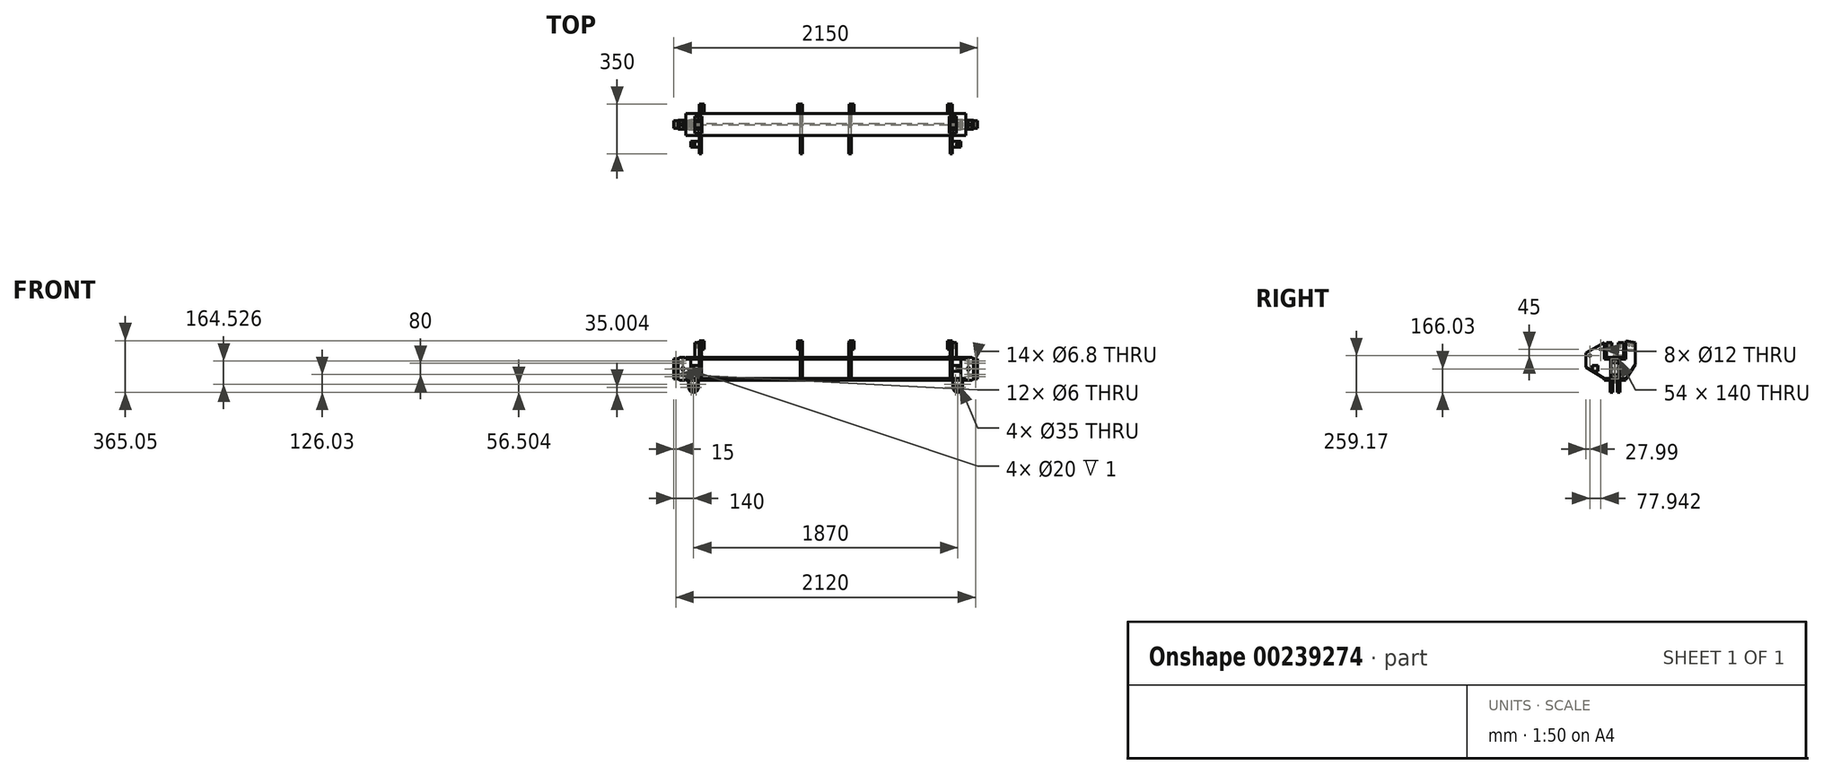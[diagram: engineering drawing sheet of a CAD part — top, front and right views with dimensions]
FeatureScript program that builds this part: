
annotation { "Feature Type Name" : "Feature", "Feature Type Description" : "" }
export const myFeature = defineFeature(function(context is Context, id is Id, definition is map)
    precondition{}
    {
        {
            var Q0;
            Q0=qCreatedBy(makeId("Right.planeOp"),FACE);
            var sketch = newSketch(context, id + "F0", { "sketchPlane" : qUnion([Q0])});
            skLineSegment(sketch, "E0.bottom", {"start": v(-77.22, 81.03) * mm, "end": v(77.22, 81.03) * mm});
            skLineSegment(sketch, "E0.top", {"start": v(-77.22, -81.03) * mm, "end": v(77.22, -81.03) * mm});
            skLineSegment(sketch, "E0.left", {"start": v(-77.22, 81.03) * mm, "end": v(-77.22, 69.47) * mm});
            skLineSegment(sketch, "E0.right", {"start": v(77.22, 81.03) * mm, "end": v(77.22, 69.47) * mm});
            skPoint(sketch, "E0.middle", {"position": v(0, 0) * mm});
            skLineSegment(sketch, "E1", {"start": v(0, 87.3) * mm, "end": v(0, -92.44) * mm, "construction": true});
            skLineSegment(sketch, "E2.0", {"start": v(-77.22, 69.47) * mm, "end": v(-16.76, 69.47) * mm});
            skLineSegment(sketch, "E3.0", {"start": v(-77.22, -69.47) * mm, "end": v(-16.76, -69.47) * mm});
            skLineSegment(sketch, "E4.0", {"start": v(-4.06, 56.77) * mm, "end": v(-4.06, -56.77) * mm});
            skLineSegment(sketch, "E5.0", {"start": v(4.06, 56.77) * mm, "end": v(4.06, -56.77) * mm});
            skLineSegment(sketch, "E6.trimOffspring", {"start": v(16.76, -69.47) * mm, "end": v(77.22, -69.47) * mm});
            skLineSegment(sketch, "E7.trimOffspring", {"start": v(16.76, 69.47) * mm, "end": v(77.22, 69.47) * mm});
            skLineSegment(sketch, "E8.trimOffspring", {"start": v(-77.22, -69.47) * mm, "end": v(-77.22, -81.03) * mm});
            skLineSegment(sketch, "E9.trimOffspring", {"start": v(77.22, -69.47) * mm, "end": v(77.22, -81.03) * mm});
            skPoint(sketch, "E10.visualSharp", {"position": v(-4.06, 69.47) * mm});
            skArc(sketch, "E10.filletArc", {"start": v(-4.06, 56.77) * mm, "mid": v(-7.78, 65.75) * mm, "end": v(-16.76, 69.47) * mm});
            skPoint(sketch, "E11.visualSharp", {"position": v(4.06, 69.47) * mm});
            skArc(sketch, "E11.filletArc", {"start": v(16.76, 69.47) * mm, "mid": v(7.78, 65.75) * mm, "end": v(4.06, 56.77) * mm});
            skPoint(sketch, "E12.visualSharp", {"position": v(4.06, -69.47) * mm});
            skArc(sketch, "E12.filletArc", {"start": v(4.06, -56.77) * mm, "mid": v(7.78, -65.75) * mm, "end": v(16.76, -69.47) * mm});
            skPoint(sketch, "E13.visualSharp", {"position": v(-4.06, -69.47) * mm});
            skArc(sketch, "E13.filletArc", {"start": v(-16.76, -69.47) * mm, "mid": v(-7.78, -65.75) * mm, "end": v(-4.06, -56.77) * mm});
            skSolve(sketch);
        }
        {
            var Q0;
            Q0=qSketchRegion(id+"F0",true);
            extrude(context, id + "F1", {"entities" : qUnion([Q0]), "endBound" : BoundingType.SYMMETRIC, "depth" : 1980 * mm});
        }
        {
            var Q0;
            Q0=makeQuery(id+"F1.opExtrude","SWEPT_FACE",FACE,{"disambiguationData":[OSD([sQuery(id+"F0.wireOp",EDGE,"E4.0")])]});
            var sketch = newSketch(context, id + "F2", { "sketchPlane" : qUnion([Q0])});
            skLineSegment(sketch, "E14", {"start": v(0, 173.84) * mm, "end": v(0, -192.2) * mm, "construction": true});
            skLineSegment(sketch, "E15.0", {"start": v(-990, 69.47) * mm, "end": v(-990, -69.47) * mm, "construction": true});
            skLineSegment(sketch, "E16.0", {"start": v(990, 69.47) * mm, "end": v(-990, 69.47) * mm, "construction": true});
            skLineSegment(sketch, "E17.0", {"start": v(990, -69.47) * mm, "end": v(-990, -69.47) * mm, "construction": true});
            skPoint(sketch, "E18.orphan", {"position": v(-990, 56.77) * mm});
            skPoint(sketch, "E19.orphan", {"position": v(-990, -56.77) * mm});
            skLineSegment(sketch, "E20.bottom", {"start": v(-990, 69.47) * mm, "end": v(-955, 69.47) * mm});
            skLineSegment(sketch, "E20.top", {"start": v(-990, -69.47) * mm, "end": v(-955, -69.47) * mm});
            skLineSegment(sketch, "E20.left", {"start": v(-990, 69.47) * mm, "end": v(-990, -69.47) * mm});
            skLineSegment(sketch, "E20.right", {"start": v(-955, 69.47) * mm, "end": v(-955, -69.47) * mm});
            skLineSegment(sketch, "E21.MirrorCS", {"start": v(990, -69.47) * mm, "end": v(955, -69.47) * mm});
            skLineSegment(sketch, "E22.MirrorCS", {"start": v(990, 69.47) * mm, "end": v(955, 69.47) * mm});
            skLineSegment(sketch, "E23.MirrorCS", {"start": v(990, 69.47) * mm, "end": v(990, -69.47) * mm});
            skLineSegment(sketch, "E24.MirrorCS", {"start": v(955, 69.47) * mm, "end": v(955, -69.47) * mm});
            skPoint(sketch, "E25.MirrorP", {"position": v(990, -56.77) * mm});
            skPoint(sketch, "E26.MirrorP", {"position": v(990, 56.77) * mm});
            skLineSegment(sketch, "E27.MirrorCS", {"start": v(990, 69.47) * mm, "end": v(990, -69.47) * mm, "construction": true});
            skSolve(sketch);
        }
        {
            var Q0;
            Q0=qSketchRegion(id+"F2",true);
            extrude(context, id + "F3", {"entities" : qUnion([Q0]), "operationType" : NewBodyOperationType.REMOVE, "endBound" : BoundingType.SYMMETRIC, "oppositeDirection" : true, "depth" : 50 * mm});
        }
        {
            var Q0;
            Q0=qCreatedBy(makeId("Front.planeOp"),FACE);
            var sketch = newSketch(context, id + "F4", { "sketchPlane" : qUnion([Q0])});
            skLineSegment(sketch, "E28", {"start": v(0, 276.7) * mm, "end": v(0, -349.05) * mm, "construction": true});
            skLineSegment(sketch, "E29.0", {"start": v(-1075, 276.7) * mm, "end": v(-1075, -349.05) * mm, "construction": true});
            skLineSegment(sketch, "E30.0", {"start": v(990, 81.03) * mm, "end": v(-1045, 81.03) * mm, "construction": true});
            skLineSegment(sketch, "E31.0", {"start": v(990, -81.03) * mm, "end": v(-1045, -81.03) * mm, "construction": true});
            skLineSegment(sketch, "E32.0", {"start": v(-955, -69.47) * mm, "end": v(-955, 69.47) * mm, "construction": true});
            skLineSegment(sketch, "E33.0", {"start": v(990, -69.47) * mm, "end": v(-990, -69.47) * mm, "construction": true});
            skLineSegment(sketch, "E34.0", {"start": v(990, 69.47) * mm, "end": v(-990, 69.47) * mm, "construction": true});
            skPoint(sketch, "E35.orphan", {"position": v(-955, 56.77) * mm});
            skPoint(sketch, "E36.orphan", {"position": v(-955, -56.77) * mm});
            skPoint(sketch, "E37.orphan", {"position": v(-990, 81.03) * mm});
            skPoint(sketch, "E38.orphan", {"position": v(-990, -81.03) * mm});
            skLineSegment(sketch, "E39", {"start": v(-990, 81.03) * mm, "end": v(-990, 69.47) * mm, "construction": true});
            skLineSegment(sketch, "E40.0", {"start": v(-1045, 81.03) * mm, "end": v(-1045, 70) * mm, "construction": true});
            skLineSegment(sketch, "E41", {"start": v(0, 0) * mm, "end": v(-1199.42, 0) * mm, "construction": true});
            skLineSegment(sketch, "E42.0", {"start": v(0, 70) * mm, "end": v(-990, 70) * mm, "construction": true});
            skLineSegment(sketch, "E43.trimOffspring", {"start": v(-1045, 70) * mm, "end": v(-1075, 70) * mm, "construction": true});
            skLineSegment(sketch, "E44.MirrorCS", {"start": v(-1045, -70) * mm, "end": v(-1075, -70) * mm, "construction": true});
            skPoint(sketch, "E45.orphan", {"position": v(-1199.42, 70) * mm});
            skPoint(sketch, "E46.orphan", {"position": v(-1199.42, -70) * mm});
            skLineSegment(sketch, "E47.trimOffspring", {"start": v(-1045, -70) * mm, "end": v(-1045, -81.03) * mm, "construction": true});
            skLineSegment(sketch, "E48.trimOffspring", {"start": v(-990, -69.47) * mm, "end": v(-990, -81.03) * mm, "construction": true});
            skLineSegment(sketch, "E49.bottom", {"start": v(-1075, 70) * mm, "end": v(-1045, 70) * mm});
            skLineSegment(sketch, "E49.top", {"start": v(-1075, -70) * mm, "end": v(-1045, -70) * mm});
            skLineSegment(sketch, "E49.left", {"start": v(-1075, 70) * mm, "end": v(-1075, -70) * mm});
            skLineSegment(sketch, "E50.bottom", {"start": v(-1045, 81.03) * mm, "end": v(-990, 81.03) * mm});
            skLineSegment(sketch, "E50.top", {"start": v(-1045, -81.03) * mm, "end": v(-990, -81.03) * mm});
            skLineSegment(sketch, "E50.left", {"start": v(-1045, 81.03) * mm, "end": v(-1045, 70) * mm});
            skLineSegment(sketch, "E50.right", {"start": v(-990, 81.03) * mm, "end": v(-990, 69.47) * mm});
            skLineSegment(sketch, "E51.bottom", {"start": v(-990, 70) * mm, "end": v(-955, 70) * mm});
            skLineSegment(sketch, "E51.top", {"start": v(-990, -69.47) * mm, "end": v(-955, -69.47) * mm});
            skLineSegment(sketch, "E51.left", {"start": v(-990, 70) * mm, "end": v(-990, 69.47) * mm});
            skLineSegment(sketch, "E51.right", {"start": v(-955, 70) * mm, "end": v(-955, -69.47) * mm});
            skLineSegment(sketch, "E52.trimOffspring", {"start": v(-990, -69.47) * mm, "end": v(-990, -81.03) * mm});
            skLineSegment(sketch, "E53.trimOffspring", {"start": v(-1045, -70) * mm, "end": v(-1045, -81.03) * mm});
            skSolve(sketch);
        }
        {
            var Q0;
            Q0=qSketchRegion(id+"F4",true);
            extrude(context, id + "F5", {"entities" : qUnion([Q0]), "endBound" : BoundingType.SYMMETRIC, "depth" : 63.5 * mm});
        }
        {
            var Q0;
            Q0=makeQuery(id+"F5.opExtrude","SWEPT_FACE",FACE,{"disambiguationData":[OSD([sQuery(id+"F4.wireOp",EDGE,"E49.bottom")])]});
            var sketch = newSketch(context, id + "F6", { "sketchPlane" : qUnion([Q0])});
            skLineSegment(sketch, "E54", {"start": v(-948.4, 0) * mm, "end": v(-1101.52, 0) * mm, "construction": true});
            skLineSegment(sketch, "E55.0", {"start": v(-1045, -31.75) * mm, "end": v(-1045, 31.75) * mm, "construction": true});
            skLineSegment(sketch, "E56.0", {"start": v(-948.4, 27) * mm, "end": v(-1101.52, 27) * mm, "construction": true});
            skLineSegment(sketch, "E57.bottom", {"start": v(-1075, 31.75) * mm, "end": v(-1045, 31.75) * mm});
            skLineSegment(sketch, "E57.top", {"start": v(-1075, 27) * mm, "end": v(-1045, 27) * mm});
            skLineSegment(sketch, "E57.left", {"start": v(-1075, 31.75) * mm, "end": v(-1075, 27) * mm});
            skLineSegment(sketch, "E57.right", {"start": v(-1045, 31.75) * mm, "end": v(-1045, 27) * mm});
            skLineSegment(sketch, "E58.MirrorCS", {"start": v(-1045, -31.75) * mm, "end": v(-1045, -27) * mm});
            skLineSegment(sketch, "E59.MirrorCS", {"start": v(-1075, -31.75) * mm, "end": v(-1075, -27) * mm});
            skLineSegment(sketch, "E60.MirrorCS", {"start": v(-1075, -27) * mm, "end": v(-1045, -27) * mm});
            skLineSegment(sketch, "E61.MirrorCS", {"start": v(-1075, -31.75) * mm, "end": v(-1045, -31.75) * mm});
            skSolve(sketch);
        }
        {
            var Q0;
            Q0=qSketchRegion(id+"F6",true);
            extrude(context, id + "F7", {"entities" : qUnion([Q0]), "operationType" : NewBodyOperationType.REMOVE, "endBound" : BoundingType.THROUGH_ALL, "oppositeDirection" : true, "depth" : 25 * mm});
        }
        {
            var Q0;
            Q0=makeQuery(id+"F5.opExtrude","SWEPT_FACE",FACE,{"disambiguationData":[OSD([sQuery(id+"F4.wireOp",EDGE,"E50.bottom")])]});
            var sketch = newSketch(context, id + "F8", { "sketchPlane" : qUnion([Q0])});
            skLineSegment(sketch, "E62.0", {"start": v(-1075, -27) * mm, "end": v(-1075, 27) * mm, "construction": true});
            skLineSegment(sketch, "E63", {"start": v(-919.6, 0) * mm, "end": v(-1088.25, 0) * mm, "construction": true});
            skPoint(sketch, "E63.endSnap0", {"position": v(-1075, 0) * mm});
            skLineSegment(sketch, "E64.0", {"start": v(-1010, -27) * mm, "end": v(-1010, 27) * mm, "construction": true});
            skPoint(sketch, "E65", {"position": v(-1010, 0) * mm});
            skSolve(sketch);
        }
        {
            var Q0;
            Q0=sQuery(id+"F8.wireOp",VERTEX,"E65");
            var Q1;
            Q1=makeQuery(id+"F5.opExtrude","SWEPT_BODY",BODY,{"disambiguationData":[OSD([sQuery(id+"F4.wireOp",EDGE,"E49.bottom"),sQuery(id+"F4.wireOp",EDGE,"E49.top"),sQuery(id+"F4.wireOp",EDGE,"E49.left"),sQuery(id+"F4.wireOp",EDGE,"E50.bottom"),sQuery(id+"F4.wireOp",EDGE,"E50.top"),sQuery(id+"F4.wireOp",EDGE,"E50.left"),sQuery(id+"F4.wireOp",EDGE,"E50.right"),sQuery(id+"F4.wireOp",EDGE,"E51.bottom"),sQuery(id+"F4.wireOp",EDGE,"E51.top"),sQuery(id+"F4.wireOp",EDGE,"E51.right"),sQuery(id+"F4.wireOp",EDGE,"E52.trimOffspring"),sQuery(id+"F4.wireOp",EDGE,"E53.trimOffspring")])]});
            hole(context, id + "F9", {"style" : HoleStyle.SIMPLE, "endStyle" : HoleEndStyle.BLIND, "standardTappedOrClearance" : lookupTablePath({ "standard" : "ISO", "size" : "6", "type" : "Drilled" }), "standardBlindInLast" : lookupTablePath({ "standard" : "ISO", "size" : "6", "type" : "Drilled" }), "holeDiameter" : 6 * mm, "holeDepth" : 125 * mm, "locations" : qUnion([Q0]), "scope" : qUnion([Q1])});
        }
        {
            var Q0;
            Q0=sQuery(id+"F8.wireOp",VERTEX,"E65");
            var Q1;
            Q1=makeQuery(id+"F5.opExtrude","SWEPT_BODY",BODY,{"disambiguationData":[OSD([sQuery(id+"F4.wireOp",EDGE,"E49.bottom"),sQuery(id+"F4.wireOp",EDGE,"E49.top"),sQuery(id+"F4.wireOp",EDGE,"E49.left"),sQuery(id+"F4.wireOp",EDGE,"E50.bottom"),sQuery(id+"F4.wireOp",EDGE,"E50.top"),sQuery(id+"F4.wireOp",EDGE,"E50.left"),sQuery(id+"F4.wireOp",EDGE,"E50.right"),sQuery(id+"F4.wireOp",EDGE,"E51.bottom"),sQuery(id+"F4.wireOp",EDGE,"E51.top"),sQuery(id+"F4.wireOp",EDGE,"E51.right"),sQuery(id+"F4.wireOp",EDGE,"E52.trimOffspring"),sQuery(id+"F4.wireOp",EDGE,"E53.trimOffspring")])]});
            hole(context, id + "F10", {"style" : HoleStyle.SIMPLE, "endStyle" : HoleEndStyle.BLIND, "standardTappedOrClearance" : lookupTablePath({ "standard" : "ANSI", "engagement" : "75%", "pitch" : "13 tpi", "size" : "1/2", "type" : "Tapped" }), "standardBlindInLast" : lookupTablePath({ "standard" : "ANSI", "engagement" : "75%", "pitch" : "13 tpi", "size" : "1/2", "type" : "Tapped" }), "holeDiameter" : 10.72 * mm, "holeDepth" : 15 * mm, "locations" : qUnion([Q0]), "scope" : qUnion([Q1]), "majorDiameter" : 12.7 * mm});
        }
        {
            var Q0;
            {var subQ0=sQuery(id+"F4.wireOp",EDGE,"E50.bottom");Q0=makeQuery(id+"F8.imprint","IMPRINT",FACE,{"disambiguationData":[TD([[makeQuery(id+"F8.imprint","IMPRINT",EDGE,{"derivedFrom":makeQuery(id+"F5.opExtrude","CAP_EDGE",EDGE,{"disambiguationData":[OSD([subQ0])],"isStart":true})}),-1.0]])]});}
            var sketch = newSketch(context, id + "F11", { "sketchPlane" : qUnion([Q0])});
            skPoint(sketch, "E66.0", {"position": v(-1010, 0) * mm});
            skCircle(sketch, "E67", {"center": v(-1010, 0) * mm, "radius": 10 * mm});
            skSolve(sketch);
        }
        {
            var Q0;
            Q0=qSketchRegion(id+"F11",true);
            extrude(context, id + "F12", {"entities" : qUnion([Q0]), "operationType" : NewBodyOperationType.REMOVE, "oppositeDirection" : true, "depth" : 1 * mm});
        }
        {
            var Q0;
            Q0=makeQuery(id+"F5.opExtrude","SWEPT_EDGE",EDGE,{"disambiguationData":[OSD([sQuery(id+"F4.wireOp",EDGE,"E50.bottom"),sQuery(id+"F4.wireOp",EDGE,"E50.left")])]});
            var Q1;
            Q1=makeQuery(id+"F7.boolean.opBoolean","INTERSECT",EDGE,{"derivedFrom":[makeQuery(id+"F7.opExtrude","SWEPT_FACE",FACE,{"disambiguationData":[OSD([sQuery(id+"F6.wireOp",EDGE,"E57.right")])]}),makeQuery(id+"F7.opExtrude","SWEPT_FACE",FACE,{"disambiguationData":[OSD([sQuery(id+"F6.wireOp",EDGE,"E58.MirrorCS")])]})]});
            chamfer(context, id + "F13", {"entities" : qUnion([Q0, Q1]), "width" : 11 * mm, "tangentPropagation" : true});
        }
        {
            var Q0;
            Q0=makeQuery(id+"F5.opExtrude","CAP_FACE",FACE,{"disambiguationData":[OSD([sQuery(id+"F4.wireOp",EDGE,"E49.bottom"),sQuery(id+"F4.wireOp",EDGE,"E49.top"),sQuery(id+"F4.wireOp",EDGE,"E49.left"),sQuery(id+"F4.wireOp",EDGE,"E50.bottom"),sQuery(id+"F4.wireOp",EDGE,"E50.top"),sQuery(id+"F4.wireOp",EDGE,"E50.left"),sQuery(id+"F4.wireOp",EDGE,"E50.right"),sQuery(id+"F4.wireOp",EDGE,"E51.bottom"),sQuery(id+"F4.wireOp",EDGE,"E51.top"),sQuery(id+"F4.wireOp",EDGE,"E51.right"),sQuery(id+"F4.wireOp",EDGE,"E52.trimOffspring"),sQuery(id+"F4.wireOp",EDGE,"E53.trimOffspring")])],"isStart":false});
            var sketch = newSketch(context, id + "F14", { "sketchPlane" : qUnion([Q0])});
            skLineSegment(sketch, "E68", {"start": v(-947.26, 0.27) * mm, "end": v(-1104.17, 0.27) * mm, "construction": true});
            skPoint(sketch, "E68.startSnap0", {"position": v(-955, 0.27) * mm});
            skLineSegment(sketch, "E69.0", {"start": v(-1075, -70) * mm, "end": v(-1075, 70) * mm, "construction": true});
            skLineSegment(sketch, "E70.0", {"start": v(-1010, -70) * mm, "end": v(-1010, 70) * mm, "construction": true});
            skPoint(sketch, "E71", {"position": v(-1010, 0.27) * mm});
            skSolve(sketch);
        }
        {
            var Q0;
            Q0=sQuery(id+"F14.wireOp",VERTEX,"E71");
            var Q1;
            Q1=makeQuery(id+"F5.opExtrude","SWEPT_BODY",BODY,{"disambiguationData":[OSD([sQuery(id+"F4.wireOp",EDGE,"E49.bottom"),sQuery(id+"F4.wireOp",EDGE,"E49.top"),sQuery(id+"F4.wireOp",EDGE,"E49.left"),sQuery(id+"F4.wireOp",EDGE,"E50.bottom"),sQuery(id+"F4.wireOp",EDGE,"E50.top"),sQuery(id+"F4.wireOp",EDGE,"E50.left"),sQuery(id+"F4.wireOp",EDGE,"E50.right"),sQuery(id+"F4.wireOp",EDGE,"E51.bottom"),sQuery(id+"F4.wireOp",EDGE,"E51.top"),sQuery(id+"F4.wireOp",EDGE,"E51.right"),sQuery(id+"F4.wireOp",EDGE,"E52.trimOffspring"),sQuery(id+"F4.wireOp",EDGE,"E53.trimOffspring")])]});
            hole(context, id + "F15", {"style" : HoleStyle.SIMPLE, "endStyle" : HoleEndStyle.BLIND, "standardTappedOrClearance" : lookupTablePath({ "standard" : "ANSI", "engagement" : "75%", "pitch" : "13 tpi", "size" : "1/2", "type" : "Tapped" }), "standardBlindInLast" : lookupTablePath({ "standard" : "ANSI", "engagement" : "75%", "pitch" : "13 tpi", "size" : "1/2", "type" : "Tapped" }), "holeDiameter" : 10.72 * mm, "holeDepth" : 15 * mm, "locations" : qUnion([Q0]), "scope" : qUnion([Q1]), "majorDiameter" : 12.7 * mm});
        }
        {
            var Q0;
            Q0=sQuery(id+"F14.wireOp",VERTEX,"E71");
            var Q1;
            Q1=makeQuery(id+"F5.opExtrude","SWEPT_BODY",BODY,{"disambiguationData":[OSD([sQuery(id+"F4.wireOp",EDGE,"E49.bottom"),sQuery(id+"F4.wireOp",EDGE,"E49.top"),sQuery(id+"F4.wireOp",EDGE,"E49.left"),sQuery(id+"F4.wireOp",EDGE,"E50.bottom"),sQuery(id+"F4.wireOp",EDGE,"E50.top"),sQuery(id+"F4.wireOp",EDGE,"E50.left"),sQuery(id+"F4.wireOp",EDGE,"E50.right"),sQuery(id+"F4.wireOp",EDGE,"E51.bottom"),sQuery(id+"F4.wireOp",EDGE,"E51.top"),sQuery(id+"F4.wireOp",EDGE,"E51.right"),sQuery(id+"F4.wireOp",EDGE,"E52.trimOffspring"),sQuery(id+"F4.wireOp",EDGE,"E53.trimOffspring")])]});
            hole(context, id + "F16", {"style" : HoleStyle.SIMPLE, "endStyle" : HoleEndStyle.THROUGH, "standardTappedOrClearance" : lookupTablePath({ "standard" : "ISO", "size" : "6", "type" : "Drilled" }), "standardBlindInLast" : lookupTablePath({ "standard" : "ISO", "size" : "6", "type" : "Drilled" }), "holeDiameter" : 6 * mm, "locations" : qUnion([Q0]), "scope" : qUnion([Q1]), "isTappedThrough" : true});
        }
        {
            var Q0;
            {var subQ4=sQuery(id+"F4.wireOp",EDGE,"E50.right");Q0=makeQuery(id+"F14.imprint","IMPRINT",FACE,{"disambiguationData":[TD([[makeQuery(id+"F14.imprint","IMPRINT",EDGE,{"derivedFrom":makeQuery(id+"F5.opExtrude","CAP_EDGE",EDGE,{"disambiguationData":[OSD([subQ4])],"isStart":false})}),-1.0]])]});}
            var sketch = newSketch(context, id + "F17", { "sketchPlane" : qUnion([Q0])});
            skCircle(sketch, "E72", {"center": v(-1010, 0.27) * mm, "radius": 10 * mm});
            skSolve(sketch);
        }
        {
            var Q0;
            Q0=qSketchRegion(id+"F17",true);
            extrude(context, id + "F18", {"entities" : qUnion([Q0]), "operationType" : NewBodyOperationType.REMOVE, "oppositeDirection" : true, "depth" : 1 * mm});
        }
        {
            var Q0;
            Q0=makeQuery(id+"F5.opExtrude","CAP_FACE",FACE,{"disambiguationData":[OSD([sQuery(id+"F4.wireOp",EDGE,"E49.bottom"),sQuery(id+"F4.wireOp",EDGE,"E49.top"),sQuery(id+"F4.wireOp",EDGE,"E49.left"),sQuery(id+"F4.wireOp",EDGE,"E50.bottom"),sQuery(id+"F4.wireOp",EDGE,"E50.top"),sQuery(id+"F4.wireOp",EDGE,"E50.left"),sQuery(id+"F4.wireOp",EDGE,"E50.right"),sQuery(id+"F4.wireOp",EDGE,"E51.bottom"),sQuery(id+"F4.wireOp",EDGE,"E51.top"),sQuery(id+"F4.wireOp",EDGE,"E51.right"),sQuery(id+"F4.wireOp",EDGE,"E52.trimOffspring"),sQuery(id+"F4.wireOp",EDGE,"E53.trimOffspring")])],"isStart":true});
            var sketch = newSketch(context, id + "F19", { "sketchPlane" : qUnion([Q0])});
            skCircle(sketch, "E73.0", {"center": v(1010, 0.27) * mm, "radius": 10 * mm, "construction": true});
            skCircle(sketch, "E74", {"center": v(1010, 0.27) * mm, "radius": 10 * mm});
            skSolve(sketch);
        }
        {
            var Q0;
            Q0=qSketchRegion(id+"F19",true);
            extrude(context, id + "F20", {"entities" : qUnion([Q0]), "operationType" : NewBodyOperationType.REMOVE, "oppositeDirection" : true, "depth" : 1 * mm});
        }
        {
            var Q0;
            Q0=sQuery(id+"F19.wireOp",VERTEX,"E73.0.center");
            var Q1;
            Q1=makeQuery(id+"F5.opExtrude","SWEPT_BODY",BODY,{"disambiguationData":[OSD([sQuery(id+"F4.wireOp",EDGE,"E49.bottom"),sQuery(id+"F4.wireOp",EDGE,"E49.top"),sQuery(id+"F4.wireOp",EDGE,"E49.left"),sQuery(id+"F4.wireOp",EDGE,"E50.bottom"),sQuery(id+"F4.wireOp",EDGE,"E50.top"),sQuery(id+"F4.wireOp",EDGE,"E50.left"),sQuery(id+"F4.wireOp",EDGE,"E50.right"),sQuery(id+"F4.wireOp",EDGE,"E51.bottom"),sQuery(id+"F4.wireOp",EDGE,"E51.top"),sQuery(id+"F4.wireOp",EDGE,"E51.right"),sQuery(id+"F4.wireOp",EDGE,"E52.trimOffspring"),sQuery(id+"F4.wireOp",EDGE,"E53.trimOffspring")])]});
            hole(context, id + "F21", {"style" : HoleStyle.SIMPLE, "endStyle" : HoleEndStyle.BLIND, "standardTappedOrClearance" : lookupTablePath({ "standard" : "ANSI", "engagement" : "75%", "pitch" : "13 tpi", "size" : "1/2", "type" : "Tapped" }), "standardBlindInLast" : lookupTablePath({ "standard" : "ANSI", "engagement" : "75%", "pitch" : "13 tpi", "size" : "1/2", "type" : "Tapped" }), "holeDiameter" : 10.72 * mm, "holeDepth" : 15 * mm, "locations" : qUnion([Q0]), "scope" : qUnion([Q1]), "majorDiameter" : 12.7 * mm});
        }
        {
            var Q0;
            Q0=makeQuery(id+"F7.boolean.opBoolean","COPY",FACE,{"derivedFrom":makeQuery(id+"F7.opExtrude","SWEPT_FACE",FACE,{"disambiguationData":[OSD([sQuery(id+"F6.wireOp",EDGE,"E60.MirrorCS")])]})});
            var sketch = newSketch(context, id + "F22", { "sketchPlane" : qUnion([Q0])});
            skLineSegment(sketch, "E75.0", {"start": v(-1075, -70) * mm, "end": v(-1075, 70) * mm, "construction": true});
            skLineSegment(sketch, "E76.0", {"start": v(-1060, -70) * mm, "end": v(-1060, 70) * mm, "construction": true});
            skLineSegment(sketch, "E77", {"start": v(-1060, 0) * mm, "end": v(-1136.9, 0) * mm, "construction": true});
            skLineSegment(sketch, "E78.0", {"start": v(-1060, 55) * mm, "end": v(-1136.9, 55) * mm, "construction": true});
            skLineSegment(sketch, "E79.0", {"start": v(-1060, -55) * mm, "end": v(-1136.9, -55) * mm, "construction": true});
            skPoint(sketch, "E80", {"position": v(-1060, 55) * mm});
            skPoint(sketch, "E81", {"position": v(-1060, 0) * mm});
            skPoint(sketch, "E82", {"position": v(-1060, -55) * mm});
            skSolve(sketch);
        }
        {
            var Q0;
            Q0=sQuery(id+"F22.wireOp",VERTEX,"E80");
            var Q1;
            Q1=sQuery(id+"F22.wireOp",VERTEX,"E81");
            var Q2;
            Q2=sQuery(id+"F22.wireOp",VERTEX,"E82");
            var Q3;
            Q3=makeQuery(id+"F5.opExtrude","SWEPT_BODY",BODY,{"disambiguationData":[OSD([sQuery(id+"F4.wireOp",EDGE,"E49.bottom"),sQuery(id+"F4.wireOp",EDGE,"E49.top"),sQuery(id+"F4.wireOp",EDGE,"E49.left"),sQuery(id+"F4.wireOp",EDGE,"E50.bottom"),sQuery(id+"F4.wireOp",EDGE,"E50.top"),sQuery(id+"F4.wireOp",EDGE,"E50.left"),sQuery(id+"F4.wireOp",EDGE,"E50.right"),sQuery(id+"F4.wireOp",EDGE,"E51.bottom"),sQuery(id+"F4.wireOp",EDGE,"E51.top"),sQuery(id+"F4.wireOp",EDGE,"E51.right"),sQuery(id+"F4.wireOp",EDGE,"E52.trimOffspring"),sQuery(id+"F4.wireOp",EDGE,"E53.trimOffspring")])]});
            hole(context, id + "F23", {"style" : HoleStyle.SIMPLE, "endStyle" : HoleEndStyle.THROUGH, "standardTappedOrClearance" : lookupTablePath({ "standard" : "ISO", "engagement" : "75%", "pitch" : "1.25 mm", "size" : "M8", "type" : "Tapped" }), "standardBlindInLast" : lookupTablePath({ "standard" : "ISO", "engagement" : "75%", "pitch" : "1.25 mm", "size" : "M8", "type" : "Tapped" }), "holeDiameter" : 6.8 * mm, "locations" : qUnion([Q0, Q1, Q2]), "scope" : qUnion([Q3]), "isTappedThrough" : true, "majorDiameter" : 8 * mm, "showTappedDepth" : true});
        }
        {
            var Q0;
            Q0=makeQuery(id+"F7.boolean.opBoolean","COPY",FACE,{"derivedFrom":makeQuery(id+"F7.opExtrude","SWEPT_FACE",FACE,{"disambiguationData":[OSD([sQuery(id+"F6.wireOp",EDGE,"E60.MirrorCS")])]})});
            var sketch = newSketch(context, id + "F24", { "sketchPlane" : qUnion([Q0])});
            skLineSegment(sketch, "E83.0", {"start": v(-1060, 0) * mm, "end": v(-1136.9, 0) * mm, "construction": true});
            skLineSegment(sketch, "E84.0", {"start": v(-1060, -70) * mm, "end": v(-1060, 70) * mm, "construction": true});
            skLineSegment(sketch, "E85.0", {"start": v(-1060, 40) * mm, "end": v(-1136.9, 40) * mm, "construction": true});
            skPoint(sketch, "E86", {"position": v(-1060, 40) * mm});
            skPoint(sketch, "E87.MirrorP", {"position": v(-1060, -40) * mm});
            skSolve(sketch);
        }
        {
            var Q0;
            Q0=sQuery(id+"F24.wireOp",VERTEX,"E86");
            var Q1;
            Q1=sQuery(id+"F24.wireOp",VERTEX,"E87.MirrorP");
            var Q2;
            Q2=makeQuery(id+"F5.opExtrude","SWEPT_BODY",BODY,{"disambiguationData":[OSD([sQuery(id+"F4.wireOp",EDGE,"E49.bottom"),sQuery(id+"F4.wireOp",EDGE,"E49.top"),sQuery(id+"F4.wireOp",EDGE,"E49.left"),sQuery(id+"F4.wireOp",EDGE,"E50.bottom"),sQuery(id+"F4.wireOp",EDGE,"E50.top"),sQuery(id+"F4.wireOp",EDGE,"E50.left"),sQuery(id+"F4.wireOp",EDGE,"E50.right"),sQuery(id+"F4.wireOp",EDGE,"E51.bottom"),sQuery(id+"F4.wireOp",EDGE,"E51.top"),sQuery(id+"F4.wireOp",EDGE,"E51.right"),sQuery(id+"F4.wireOp",EDGE,"E52.trimOffspring"),sQuery(id+"F4.wireOp",EDGE,"E53.trimOffspring")])]});
            hole(context, id + "F25", {"style" : HoleStyle.SIMPLE, "endStyle" : HoleEndStyle.THROUGH, "standardTappedOrClearance" : lookupTablePath({ "standard" : "ISO", "size" : "6", "type" : "Drilled" }), "standardBlindInLast" : lookupTablePath({ "standard" : "ISO", "size" : "6", "type" : "Drilled" }), "holeDiameter" : 6 * mm, "locations" : qUnion([Q0, Q1]), "scope" : qUnion([Q2]), "isTappedThrough" : true});
        }
        {
            var Q0;
            Q0=makeQuery(id+"F5.opExtrude","SWEPT_FACE",FACE,{"disambiguationData":[OSD([sQuery(id+"F4.wireOp",EDGE,"E49.left")])]});
            var sketch = newSketch(context, id + "F26", { "sketchPlane" : qUnion([Q0])});
            skLineSegment(sketch, "E88.0.0", {"start": v(-27, -70) * mm, "end": v(27, -70) * mm, "construction": true});
            skLineSegment(sketch, "E88.0.1", {"start": v(27, -70) * mm, "end": v(27, 70) * mm, "construction": true});
            skLineSegment(sketch, "E88.0.2", {"start": v(27, 70) * mm, "end": v(-27, 70) * mm, "construction": true});
            skLineSegment(sketch, "E88.0.3", {"start": v(-27, 70) * mm, "end": v(-27, -70) * mm, "construction": true});
            skLineSegment(sketch, "E89", {"start": v(-27, 0) * mm, "end": v(56.48, 0) * mm, "construction": true});
            skPoint(sketch, "E89.endSnap0", {"position": v(-27, 0) * mm});
            skLineSegment(sketch, "E90", {"start": v(0, 96.87) * mm, "end": v(0, -94.28) * mm, "construction": true});
            skLineSegment(sketch, "E91.0", {"start": v(-27, -40) * mm, "end": v(56.48, -40) * mm, "construction": true});
            skPoint(sketch, "E92", {"position": v(0, -40) * mm});
            skPoint(sketch, "E93.MirrorP", {"position": v(0, 40) * mm});
            skSolve(sketch);
        }
        {
            var Q0;
            Q0=sQuery(id+"F26.wireOp",VERTEX,"E93.MirrorP");
            var Q1;
            Q1=sQuery(id+"F26.wireOp",VERTEX,"E92");
            var Q2;
            Q2=makeQuery(id+"F5.opExtrude","SWEPT_BODY",BODY,{"disambiguationData":[OSD([sQuery(id+"F4.wireOp",EDGE,"E49.bottom"),sQuery(id+"F4.wireOp",EDGE,"E49.top"),sQuery(id+"F4.wireOp",EDGE,"E49.left"),sQuery(id+"F4.wireOp",EDGE,"E50.bottom"),sQuery(id+"F4.wireOp",EDGE,"E50.top"),sQuery(id+"F4.wireOp",EDGE,"E50.left"),sQuery(id+"F4.wireOp",EDGE,"E50.right"),sQuery(id+"F4.wireOp",EDGE,"E51.bottom"),sQuery(id+"F4.wireOp",EDGE,"E51.top"),sQuery(id+"F4.wireOp",EDGE,"E51.right"),sQuery(id+"F4.wireOp",EDGE,"E52.trimOffspring"),sQuery(id+"F4.wireOp",EDGE,"E53.trimOffspring")])]});
            hole(context, id + "F27", {"style" : HoleStyle.SIMPLE, "endStyle" : HoleEndStyle.BLIND, "standardTappedOrClearance" : lookupTablePath({ "standard" : "ISO", "size" : "6", "type" : "Drilled" }), "standardBlindInLast" : lookupTablePath({ "standard" : "ISO", "size" : "6", "type" : "Drilled" }), "holeDiameter" : 6 * mm, "holeDepth" : 65 * mm, "locations" : qUnion([Q0, Q1]), "scope" : qUnion([Q2])});
        }
        {
            var Q0;
            Q0=sQuery(id+"F26.wireOp",VERTEX,"E93.MirrorP");
            var Q1;
            Q1=sQuery(id+"F26.wireOp",VERTEX,"E92");
            var Q2;
            Q2=makeQuery(id+"F5.opExtrude","SWEPT_BODY",BODY,{"disambiguationData":[OSD([sQuery(id+"F4.wireOp",EDGE,"E49.bottom"),sQuery(id+"F4.wireOp",EDGE,"E49.top"),sQuery(id+"F4.wireOp",EDGE,"E49.left"),sQuery(id+"F4.wireOp",EDGE,"E50.bottom"),sQuery(id+"F4.wireOp",EDGE,"E50.top"),sQuery(id+"F4.wireOp",EDGE,"E50.left"),sQuery(id+"F4.wireOp",EDGE,"E50.right"),sQuery(id+"F4.wireOp",EDGE,"E51.bottom"),sQuery(id+"F4.wireOp",EDGE,"E51.top"),sQuery(id+"F4.wireOp",EDGE,"E51.right"),sQuery(id+"F4.wireOp",EDGE,"E52.trimOffspring"),sQuery(id+"F4.wireOp",EDGE,"E53.trimOffspring")])]});
            hole(context, id + "F28", {"style" : HoleStyle.SIMPLE, "endStyle" : HoleEndStyle.BLIND, "standardTappedOrClearance" : lookupTablePath({ "standard" : "ISO", "engagement" : "75%", "pitch" : "1.25 mm", "size" : "M8", "type" : "Tapped" }), "standardBlindInLast" : lookupTablePath({ "standard" : "ISO", "engagement" : "75%", "pitch" : "1.25 mm", "size" : "M8", "type" : "Tapped" }), "holeDiameter" : 6.8 * mm, "holeDepth" : 12 * mm, "locations" : qUnion([Q0, Q1]), "scope" : qUnion([Q2]), "majorDiameter" : 8 * mm});
        }
        {
            var Q0;
            Q0=makeQuery(id+"F5.opExtrude","SWEPT_BODY",BODY,{"disambiguationData":[OSD([sQuery(id+"F4.wireOp",EDGE,"E49.bottom"),sQuery(id+"F4.wireOp",EDGE,"E49.top"),sQuery(id+"F4.wireOp",EDGE,"E49.left"),sQuery(id+"F4.wireOp",EDGE,"E50.bottom"),sQuery(id+"F4.wireOp",EDGE,"E50.top"),sQuery(id+"F4.wireOp",EDGE,"E50.left"),sQuery(id+"F4.wireOp",EDGE,"E50.right"),sQuery(id+"F4.wireOp",EDGE,"E51.bottom"),sQuery(id+"F4.wireOp",EDGE,"E51.top"),sQuery(id+"F4.wireOp",EDGE,"E51.right"),sQuery(id+"F4.wireOp",EDGE,"E52.trimOffspring"),sQuery(id+"F4.wireOp",EDGE,"E53.trimOffspring")])]});
            var Q1;
            Q1=qCreatedBy(makeId("Right.planeOp"),FACE);
            mirror(context, id + "F29", {"entities" : qUnion([Q0]), "mirrorPlane" : qUnion([Q1])});
        }
        {
            var Q0;
            Q0=qCreatedBy(makeId("Front.planeOp"),FACE);
            var sketch = newSketch(context, id + "F30", { "sketchPlane" : qUnion([Q0])});
            skLineSegment(sketch, "E94", {"start": v(0, 217.37) * mm, "end": v(0, -483.51) * mm, "construction": true});
            skLineSegment(sketch, "E95.0", {"start": v(-935, 217.37) * mm, "end": v(-935, -483.51) * mm, "construction": true});
            skLineSegment(sketch, "E96.0.0", {"start": v(-990, -69.47) * mm, "end": v(-990, -81.03) * mm, "construction": true});
            skLineSegment(sketch, "E96.0.1", {"start": v(-990, -81.03) * mm, "end": v(-900, -81.03) * mm});
            skLineSegment(sketch, "E96.0.2", {"start": v(990, -81.03) * mm, "end": v(990, -69.47) * mm, "construction": true});
            skLineSegment(sketch, "E96.0.3", {"start": v(990, -69.47) * mm, "end": v(-990, -69.47) * mm, "construction": true});
            skLineSegment(sketch, "E97.0", {"start": v(-990, -131.03) * mm, "end": v(990, -131.03) * mm, "construction": true});
            skCircle(sketch, "E98", {"center": v(-935, -131.03) * mm, "radius": 17.5 * mm});
            skArc(sketch, "E99", {"start": v(-970, -131.03) * mm, "mid": v(-935, -166.03) * mm, "end": v(-900, -131.03) * mm});
            skLineSegment(sketch, "E100", {"start": v(-970, -131.03) * mm, "end": v(-970, -81.03) * mm});
            skLineSegment(sketch, "E101", {"start": v(-900, -131.03) * mm, "end": v(-900, -81.03) * mm});
            skLineSegment(sketch, "E102.trimOffspring", {"start": v(0, -81.03) * mm, "end": v(990, -81.03) * mm});
            skLineSegment(sketch, "E103", {"start": v(-935, -166.03) * mm, "end": v(-989.6, -166.03) * mm, "construction": true});
            skLineSegment(sketch, "E104.0", {"start": v(-935, -144.53) * mm, "end": v(-989.6, -144.53) * mm, "construction": true});
            skLineSegment(sketch, "E105.0", {"start": v(-990, -109.53) * mm, "end": v(990, -109.53) * mm, "construction": true});
            skLineSegment(sketch, "E106.0", {"start": v(-953, 217.37) * mm, "end": v(-953, -483.51) * mm, "construction": true});
            skPoint(sketch, "E107", {"position": v(-953, -109.53) * mm});
            skPoint(sketch, "E108.MirrorP", {"position": v(-917, -109.53) * mm});
            skSolve(sketch);
        }
        {
            var Q0;
            Q0=qSketchRegion(id+"F30",true);
            extrude(context, id + "F31", {"entities" : qUnion([Q0]), "endBound" : BoundingType.SYMMETRIC, "depth" : 70 * mm});
        }
        {
            var Q0;
            Q0=makeQuery(id+"F31.opExtrude","CAP_FACE",FACE,{"disambiguationData":[OSD([sQuery(id+"F30.wireOp",EDGE,"E96.0.1"),sQuery(id+"F30.wireOp",EDGE,"E98"),sQuery(id+"F30.wireOp",EDGE,"E99"),sQuery(id+"F30.wireOp",EDGE,"E100"),sQuery(id+"F30.wireOp",EDGE,"E101")])],"isStart":false});
            var sketch = newSketch(context, id + "F32", { "sketchPlane" : qUnion([Q0])});
            skPoint(sketch, "E109.0", {"position": v(-953, -109.53) * mm});
            skPoint(sketch, "E110.0", {"position": v(-917, -109.53) * mm});
            skSolve(sketch);
        }
        {
            var Q0;
            Q0=sQuery(id+"F32.wireOp",VERTEX,"E109.0");
            var Q1;
            Q1=sQuery(id+"F32.wireOp",VERTEX,"E110.0");
            var Q2;
            Q2=makeQuery(id+"F31.opExtrude","SWEPT_BODY",BODY,{"disambiguationData":[OSD([sQuery(id+"F30.wireOp",EDGE,"E96.0.1"),sQuery(id+"F30.wireOp",EDGE,"E98"),sQuery(id+"F30.wireOp",EDGE,"E99"),sQuery(id+"F30.wireOp",EDGE,"E100"),sQuery(id+"F30.wireOp",EDGE,"E101")])]});
            hole(context, id + "F33", {"style" : HoleStyle.SIMPLE, "endStyle" : HoleEndStyle.THROUGH, "standardTappedOrClearance" : lookupTablePath({ "standard" : "ISO", "engagement" : "75%", "pitch" : "1.25 mm", "size" : "M8", "type" : "Tapped" }), "standardBlindInLast" : lookupTablePath({ "standard" : "ISO", "engagement" : "75%", "pitch" : "1.25 mm", "size" : "M8", "type" : "Tapped" }), "holeDiameter" : 6.8 * mm, "locations" : qUnion([Q0, Q1]), "scope" : qUnion([Q2]), "isTappedThrough" : true, "majorDiameter" : 8 * mm, "showTappedDepth" : true});
        }
        {
            var Q0;
            Q0=makeQuery(id+"F31.opExtrude","SWEPT_FACE",FACE,{"disambiguationData":[OSD([sQuery(id+"F30.wireOp",EDGE,"E101")])]});
            var sketch = newSketch(context, id + "F34", { "sketchPlane" : qUnion([Q0])});
            skLineSegment(sketch, "E111.0", {"start": v(-35, -81.03) * mm, "end": v(35, -81.03) * mm, "construction": true});
            skLineSegment(sketch, "E112", {"start": v(0, -81.03) * mm, "end": v(0, -181.86) * mm, "construction": true});
            skPoint(sketch, "E112.endSnap0", {"position": v(0, -81.03) * mm});
            skLineSegment(sketch, "E113.0", {"start": v(-15.5, -81.03) * mm, "end": v(-15.5, -181.86) * mm, "construction": true});
            skLineSegment(sketch, "E114", {"start": v(35, -166.03) * mm, "end": v(-35, -166.03) * mm, "construction": true});
            skLineSegment(sketch, "E115.0", {"start": v(35, -148.53) * mm, "end": v(35, -113.53) * mm, "construction": true});
            skLineSegment(sketch, "E116", {"start": v(35, -131.03) * mm, "end": v(-53.23, -131.03) * mm, "construction": true});
            skLineSegment(sketch, "E117.0", {"start": v(35, -87.03) * mm, "end": v(-53.23, -87.03) * mm, "construction": true});
            skLineSegment(sketch, "E118.bottom", {"start": v(-15.5, -166.03) * mm, "end": v(15.5, -166.03) * mm});
            skLineSegment(sketch, "E118.top", {"start": v(-15.5, -87.03) * mm, "end": v(15.5, -87.03) * mm});
            skLineSegment(sketch, "E118.left", {"start": v(-15.5, -166.03) * mm, "end": v(-15.5, -87.03) * mm});
            skLineSegment(sketch, "E118.right", {"start": v(15.5, -166.03) * mm, "end": v(15.5, -87.03) * mm});
            skSolve(sketch);
        }
        {
            var Q0;
            Q0=qSketchRegion(id+"F34",true);
            extrude(context, id + "F35", {"entities" : qUnion([Q0]), "operationType" : NewBodyOperationType.REMOVE, "endBound" : BoundingType.THROUGH_ALL, "oppositeDirection" : true, "depth" : 25 * mm});
        }
        {
            var Q0;
            Q0=makeQuery(id+"F35.boolean.opBoolean","COPY",EDGE,{"derivedFrom":makeQuery(id+"F35.opExtrude","SWEPT_EDGE",EDGE,{"disambiguationData":[OSD([sQuery(id+"F34.wireOp",EDGE,"E118.top"),sQuery(id+"F34.wireOp",EDGE,"E118.right")])]})});
            var Q1;
            Q1=makeQuery(id+"F35.boolean.opBoolean","COPY",EDGE,{"derivedFrom":makeQuery(id+"F35.opExtrude","SWEPT_EDGE",EDGE,{"disambiguationData":[OSD([sQuery(id+"F34.wireOp",EDGE,"E118.top"),sQuery(id+"F34.wireOp",EDGE,"E118.left")])]})});
            fillet(context, id + "F36", {"entities" : qUnion([Q0, Q1]), "radius" : 2 * mm, "tangentPropagation" : true, "allowEdgeOverflow" : false});
        }
        {
            var Q0;
            Q0=makeQuery(id+"F31.opExtrude","SWEPT_BODY",BODY,{"disambiguationData":[OSD([sQuery(id+"F30.wireOp",EDGE,"E96.0.1"),sQuery(id+"F30.wireOp",EDGE,"E98"),sQuery(id+"F30.wireOp",EDGE,"E99"),sQuery(id+"F30.wireOp",EDGE,"E100"),sQuery(id+"F30.wireOp",EDGE,"E101")])]});
            var Q1;
            Q1=qCreatedBy(makeId("Right.planeOp"),FACE);
            mirror(context, id + "F37", {"entities" : qUnion([Q0]), "mirrorPlane" : qUnion([Q1])});
        }
        {
            var Q0;
            Q0=makeQuery(id+"F1.opExtrude","SWEPT_FACE",FACE,{"disambiguationData":[OSD([sQuery(id+"F0.wireOp",EDGE,"E0.bottom")])]});
            var sketch = newSketch(context, id + "F38", { "sketchPlane" : qUnion([Q0])});
            skLineSegment(sketch, "E119", {"start": v(0, 374.52) * mm, "end": v(0, -390.73) * mm, "construction": true});
            skLineSegment(sketch, "E120.0", {"start": v(-880, 374.52) * mm, "end": v(-880, -390.73) * mm, "construction": true});
            skLineSegment(sketch, "E121.0", {"start": v(-925, 374.52) * mm, "end": v(-925, -390.73) * mm, "construction": true});
            skLineSegment(sketch, "E122.0", {"start": v(-874.2, 374.52) * mm, "end": v(-874.2, -390.73) * mm, "construction": true});
            skPoint(sketch, "E123.endSnap0", {"position": v(0, -8.1) * mm});
            skLineSegment(sketch, "E124.0.0", {"start": v(-990, 77.22) * mm, "end": v(-990, -77.22) * mm, "construction": true});
            skLineSegment(sketch, "E124.0.1", {"start": v(-990, -77.22) * mm, "end": v(990, -77.22) * mm, "construction": true});
            skLineSegment(sketch, "E124.0.2", {"start": v(990, -77.22) * mm, "end": v(990, 77.22) * mm, "construction": true});
            skLineSegment(sketch, "E124.0.3", {"start": v(990, 77.22) * mm, "end": v(-990, 77.22) * mm, "construction": true});
            skLineSegment(sketch, "E125", {"start": v(-990, 0) * mm, "end": v(-602.18, 0) * mm, "construction": true});
            skLineSegment(sketch, "E126.0", {"start": v(-990, 60) * mm, "end": v(-602.18, 60) * mm, "construction": true});
            skLineSegment(sketch, "E127.bottom", {"start": v(-925, 60) * mm, "end": v(-874.2, 60) * mm});
            skLineSegment(sketch, "E127.top", {"start": v(-925, -60) * mm, "end": v(-874.2, -60) * mm});
            skLineSegment(sketch, "E127.left", {"start": v(-925, 60) * mm, "end": v(-925, -60) * mm});
            skLineSegment(sketch, "E127.right", {"start": v(-874.2, 60) * mm, "end": v(-874.2, -60) * mm});
            skSolve(sketch);
        }
        {
            var Q0;
            Q0=qSketchRegion(id+"F38",true);
            extrude(context, id + "F39", {"entities" : qUnion([Q0]), "depth" : 120 * mm});
        }
        {
            var Q0;
            Q0=makeQuery(id+"F39.opExtrude","SWEPT_FACE",FACE,{"disambiguationData":[OSD([sQuery(id+"F38.wireOp",EDGE,"E127.left")])]});
            var sketch = newSketch(context, id + "F40", { "sketchPlane" : qUnion([Q0])});
            skLineSegment(sketch, "E128.0", {"start": v(35, -113.53) * mm, "end": v(35, -148.53) * mm, "construction": true});
            skLineSegment(sketch, "E129", {"start": v(35, -131.03) * mm, "end": v(-153.9, -131.03) * mm, "construction": true});
            skLineSegment(sketch, "E130.0", {"start": v(35, 168.97) * mm, "end": v(-153.9, 168.97) * mm, "construction": true});
            skLineSegment(sketch, "E131.0", {"start": v(-60, 201.03) * mm, "end": v(60, 201.03) * mm});
            skLineSegment(sketch, "E132", {"start": v(0, 201.03) * mm, "end": v(0, 143.76) * mm, "construction": true});
            skPoint(sketch, "E132.endSnap0", {"position": v(0, 201.03) * mm});
            skArc(sketch, "E133", {"start": v(-22.5, 168.97) * mm, "mid": v(0, 146.47) * mm, "end": v(22.5, 168.97) * mm});
            skLineSegment(sketch, "E134.0", {"start": v(60, 185.97) * mm, "end": v(22.5, 185.97) * mm});
            skLineSegment(sketch, "E135", {"start": v(-22.5, 168.97) * mm, "end": v(-22.5, 185.97) * mm});
            skLineSegment(sketch, "E136", {"start": v(22.5, 168.97) * mm, "end": v(22.5, 185.97) * mm});
            skLineSegment(sketch, "E137.0", {"start": v(60, 201.03) * mm, "end": v(60, 185.97) * mm});
            skLineSegment(sketch, "E138.0", {"start": v(-60, 201.03) * mm, "end": v(-60, 185.97) * mm});
            skPoint(sketch, "E139.orphan", {"position": v(-60, 81.03) * mm});
            skPoint(sketch, "E140.orphan", {"position": v(60, 81.03) * mm});
            skLineSegment(sketch, "E141.trimOffspring", {"start": v(-22.5, 185.97) * mm, "end": v(-60, 185.97) * mm});
            skSolve(sketch);
        }
        {
            var Q0;
            Q0=qSketchRegion(id+"F40",true);
            extrude(context, id + "F41", {"entities" : qUnion([Q0]), "operationType" : NewBodyOperationType.REMOVE, "endBound" : BoundingType.THROUGH_ALL, "oppositeDirection" : true, "depth" : 25 * mm});
        }
        {
            var Q0;
            Q0=makeQuery(id+"F41.boolean.opBoolean","COPY",FACE,{"derivedFrom":makeQuery(id+"F41.opExtrude","SWEPT_FACE",FACE,{"disambiguationData":[OSD([sQuery(id+"F40.wireOp",EDGE,"E141.trimOffspring")])]})});
            var sketch = newSketch(context, id + "F42", { "sketchPlane" : qUnion([Q0])});
            skLineSegment(sketch, "E142.0", {"start": v(-874.2, 60) * mm, "end": v(-874.2, 22.5) * mm, "construction": true});
            skLineSegment(sketch, "E143.0", {"start": v(-874.2, -60) * mm, "end": v(-925, -60) * mm, "construction": true});
            skLineSegment(sketch, "E144.bottom", {"start": v(-874.2, 60) * mm, "end": v(-880, 60) * mm});
            skLineSegment(sketch, "E144.top", {"start": v(-874.2, -60) * mm, "end": v(-880, -60) * mm});
            skLineSegment(sketch, "E144.left", {"start": v(-874.2, 60) * mm, "end": v(-874.2, -60) * mm});
            skLineSegment(sketch, "E144.right", {"start": v(-880, 60) * mm, "end": v(-880, -60) * mm});
            skLineSegment(sketch, "E145.0", {"start": v(-925, 22.5) * mm, "end": v(-925, 60) * mm, "construction": true});
            skSolve(sketch);
        }
        {
            var Q0;
            Q0=qSketchRegion(id+"F42",true);
            extrude(context, id + "F43", {"entities" : qUnion([Q0]), "operationType" : NewBodyOperationType.REMOVE, "oppositeDirection" : true, "depth" : 92 * mm});
        }
        {
            var Q0;
            Q0=makeQuery(id+"F41.boolean.opBoolean","COPY",FACE,{"derivedFrom":makeQuery(id+"F41.opExtrude","SWEPT_FACE",FACE,{"disambiguationData":[OSD([sQuery(id+"F40.wireOp",EDGE,"E141.trimOffspring")])]})});
            var sketch = newSketch(context, id + "F44", { "sketchPlane" : qUnion([Q0])});
            skLineSegment(sketch, "E146.0.0", {"start": v(-880, 22.5) * mm, "end": v(-880, 60) * mm, "construction": true});
            skLineSegment(sketch, "E146.0.1", {"start": v(-880, 60) * mm, "end": v(-925, 60) * mm, "construction": true});
            skLineSegment(sketch, "E146.0.2", {"start": v(-925, 60) * mm, "end": v(-925, 22.5) * mm, "construction": true});
            skLineSegment(sketch, "E146.0.3", {"start": v(-925, 22.5) * mm, "end": v(-880, 22.5) * mm, "construction": true});
            skLineSegment(sketch, "E147.0.0", {"start": v(-880, -60) * mm, "end": v(-880, -22.5) * mm, "construction": true});
            skLineSegment(sketch, "E147.0.1", {"start": v(-880, -22.5) * mm, "end": v(-925, -22.5) * mm, "construction": true});
            skLineSegment(sketch, "E147.0.2", {"start": v(-925, -22.5) * mm, "end": v(-925, -60) * mm, "construction": true});
            skLineSegment(sketch, "E147.0.3", {"start": v(-925, -60) * mm, "end": v(-880, -60) * mm, "construction": true});
            skLineSegment(sketch, "E148", {"start": v(-902.5, 60) * mm, "end": v(-902.5, -60) * mm, "construction": true});
            skLineSegment(sketch, "E149", {"start": v(-902.5, 0) * mm, "end": v(-937.6, 0) * mm, "construction": true});
            skLineSegment(sketch, "E150.0", {"start": v(-902.5, 37.5) * mm, "end": v(-937.6, 37.5) * mm, "construction": true});
            skPoint(sketch, "E151", {"position": v(-902.5, 37.5) * mm});
            skPoint(sketch, "E152.MirrorP", {"position": v(-902.5, -37.5) * mm});
            skSolve(sketch);
        }
        {
            var Q0;
            Q0=sQuery(id+"F44.wireOp",VERTEX,"E151");
            var Q1;
            Q1=sQuery(id+"F44.wireOp",VERTEX,"E152.MirrorP");
            var Q2;
            Q2=makeQuery(id+"F39.opExtrude","SWEPT_BODY",BODY,{"disambiguationData":[OSD([sQuery(id+"F38.wireOp",EDGE,"E127.bottom"),sQuery(id+"F38.wireOp",EDGE,"E127.top"),sQuery(id+"F38.wireOp",EDGE,"E127.left"),sQuery(id+"F38.wireOp",EDGE,"E127.right")])]});
            hole(context, id + "F45", {"style" : HoleStyle.SIMPLE, "endStyle" : HoleEndStyle.BLIND, "standardTappedOrClearance" : lookupTablePath({ "standard" : "ISO", "engagement" : "75%", "pitch" : "1.25 mm", "size" : "M12", "type" : "Tapped" }), "standardBlindInLast" : lookupTablePath({ "standard" : "ISO", "engagement" : "75%", "pitch" : "1.25 mm", "size" : "M12", "type" : "Tapped" }), "holeDiameter" : 10.8 * mm, "holeDepth" : 35 * mm, "locations" : qUnion([Q0, Q1]), "scope" : qUnion([Q2]), "majorDiameter" : 12 * mm});
        }
        {
            var Q0;
            Q0=makeQuery(id+"F39.opExtrude","SWEPT_BODY",BODY,{"disambiguationData":[OSD([sQuery(id+"F38.wireOp",EDGE,"E127.bottom"),sQuery(id+"F38.wireOp",EDGE,"E127.top"),sQuery(id+"F38.wireOp",EDGE,"E127.left"),sQuery(id+"F38.wireOp",EDGE,"E127.right")])]});
            var Q1;
            Q1=qCreatedBy(makeId("Right.planeOp"),FACE);
            mirror(context, id + "F46", {"entities" : qUnion([Q0]), "mirrorPlane" : qUnion([Q1])});
        }
        {
            var Q0;
            Q0=qCreatedBy(makeId("Right.planeOp"),FACE);
            cPlane(context, id + "F47", {"entities" : qUnion([Q0]), "cplaneType" : CPlaneType.OFFSET, "offset" : (330 / 2 + 15) * mm, "width" : 150 * mm, "height" : 150 * mm});
        }
        {
            var Q0;
            Q0=qCreatedBy(id+"F47.planeOp",FACE);
            var sketch = newSketch(context, id + "F48", { "sketchPlane" : qUnion([Q0])});
            skLineSegment(sketch, "E153", {"start": v(0, 256.72) * mm, "end": v(0, -431.7) * mm, "construction": true});
            skLineSegment(sketch, "E154.0.0", {"start": v(-60, 81.03) * mm, "end": v(-60, 185.97) * mm, "construction": true});
            skLineSegment(sketch, "E154.0.1", {"start": v(-60, 185.97) * mm, "end": v(-22.5, 185.97) * mm, "construction": true});
            skLineSegment(sketch, "E154.0.2", {"start": v(-22.5, 185.97) * mm, "end": v(-22.5, 168.97) * mm, "construction": true});
            skArc(sketch, "E154.0.3", {"start": v(-22.5, 168.97) * mm, "mid": v(0, 146.47) * mm, "end": v(22.5, 168.97) * mm, "construction": true});
            skLineSegment(sketch, "E154.0.4", {"start": v(22.5, 168.97) * mm, "end": v(22.5, 185.97) * mm, "construction": true});
            skLineSegment(sketch, "E154.0.5", {"start": v(22.5, 185.97) * mm, "end": v(144, 185.97) * mm, "construction": true});
            skLineSegment(sketch, "E154.0.6", {"start": v(60, 185.97) * mm, "end": v(60, 81.03) * mm, "construction": true});
            skLineSegment(sketch, "E154.0.7", {"start": v(60, 81.03) * mm, "end": v(-60, 81.03) * mm, "construction": true});
            skLineSegment(sketch, "E155.0", {"start": v(144, 256.72) * mm, "end": v(144, -69.47) * mm});
            skLineSegment(sketch, "E156.0.0", {"start": v(77.22, 81.03) * mm, "end": v(77.22, 69.47) * mm, "construction": true});
            skLineSegment(sketch, "E156.0.1", {"start": v(77.22, 69.47) * mm, "end": v(-77.22, 69.47) * mm, "construction": true});
            skLineSegment(sketch, "E156.0.2", {"start": v(-77.22, 69.47) * mm, "end": v(-77.22, 81.03) * mm, "construction": true});
            skLineSegment(sketch, "E156.0.3", {"start": v(-77.22, 81.03) * mm, "end": v(77.22, 81.03) * mm, "construction": true});
            skLineSegment(sketch, "E157.0.0", {"start": v(-77.22, -69.47) * mm, "end": v(144, -69.47) * mm, "construction": true});
            skLineSegment(sketch, "E157.0.1", {"start": v(77.22, -69.47) * mm, "end": v(77.22, -81.03) * mm, "construction": true});
            skLineSegment(sketch, "E157.0.2", {"start": v(77.22, -81.03) * mm, "end": v(-77.22, -81.03) * mm, "construction": true});
            skLineSegment(sketch, "E157.0.3", {"start": v(-77.22, -81.03) * mm, "end": v(-77.22, -69.47) * mm, "construction": true});
            skLineSegment(sketch, "E158.0.0", {"start": v(16.76, -69.47) * mm, "end": v(-16.76, -69.47) * mm, "construction": true});
            skArc(sketch, "E158.0.1", {"start": v(-16.76, -69.47) * mm, "mid": v(-7.78, -65.75) * mm, "end": v(-4.06, -56.77) * mm, "construction": true});
            skLineSegment(sketch, "E158.0.2", {"start": v(-4.06, -56.77) * mm, "end": v(-4.06, 56.77) * mm, "construction": true});
            skArc(sketch, "E158.0.3", {"start": v(-4.06, 56.77) * mm, "mid": v(-7.78, 65.75) * mm, "end": v(-16.76, 69.47) * mm, "construction": true});
            skLineSegment(sketch, "E158.0.4", {"start": v(-16.76, 69.47) * mm, "end": v(16.76, 69.47) * mm, "construction": true});
            skArc(sketch, "E158.0.5", {"start": v(16.76, 69.47) * mm, "mid": v(7.78, 65.75) * mm, "end": v(4.06, 56.77) * mm, "construction": true});
            skLineSegment(sketch, "E158.0.6", {"start": v(4.06, 56.77) * mm, "end": v(4.06, -56.77) * mm, "construction": true});
            skArc(sketch, "E158.0.7", {"start": v(4.06, -56.77) * mm, "mid": v(7.78, -65.75) * mm, "end": v(16.76, -69.47) * mm, "construction": true});
            skLineSegment(sketch, "E159", {"start": v(144, 185.97) * mm, "end": v(77.22, 197.75) * mm});
            skLineSegment(sketch, "E160.0", {"start": v(70, 86.03) * mm, "end": v(77.22, 86.03) * mm, "construction": true});
            skLineSegment(sketch, "E161.0", {"start": v(77.22, 199.02) * mm, "end": v(77.22, 69.47) * mm});
            skLineSegment(sketch, "E162", {"start": v(144, 30.53) * mm, "end": v(80.74, -69.47) * mm});
            skLineSegment(sketch, "E163", {"start": v(80.74, -69.47) * mm, "end": v(16.76, -69.47) * mm});
            skLineSegment(sketch, "E164", {"start": v(16.76, -69.47) * mm, "end": v(4.06, -56.77) * mm});
            skLineSegment(sketch, "E165", {"start": v(4.06, -56.77) * mm, "end": v(4.06, 56.77) * mm});
            skLineSegment(sketch, "E166", {"start": v(4.06, 56.77) * mm, "end": v(16.76, 69.47) * mm});
            skLineSegment(sketch, "E167", {"start": v(16.76, 69.47) * mm, "end": v(77.22, 69.47) * mm});
            skLineSegment(sketch, "E168", {"start": v(77.22, 69.47) * mm, "end": v(77.22, 86.03) * mm});
            skLineSegment(sketch, "E169", {"start": v(77.22, 86.03) * mm, "end": v(70, 86.03) * mm});
            skLineSegment(sketch, "E170", {"start": v(70, 185.97) * mm, "end": v(70, 199.02) * mm});
            skLineSegment(sketch, "E171", {"start": v(144, 185.97) * mm, "end": v(144, 30.53) * mm});
            skLineSegment(sketch, "E172", {"start": v(77.22, 199.02) * mm, "end": v(91.33, 199.02) * mm});
            skLineSegment(sketch, "E173", {"start": v(77.22, 199.02) * mm, "end": v(150.28, 186.14) * mm});
            skSolve(sketch);
        }
        {
            var Q0;
            Q0=qSketchRegion(id+"F48",true);
            extrude(context, id + "F49", {"entities" : qUnion([Q0]), "oppositeDirection" : true, "depth" : 15.88 * mm});
        }
        {
            var Q0;
            Q0=makeQuery(id+"F49.opExtrude","CAP_FACE",FACE,{"disambiguationData":[OSD([sQuery(id+"F48.wireOp",EDGE,"E159"),sQuery(id+"F48.wireOp",EDGE,"E162"),sQuery(id+"F48.wireOp",EDGE,"E163"),sQuery(id+"F48.wireOp",EDGE,"E164"),sQuery(id+"F48.wireOp",EDGE,"E165"),sQuery(id+"F48.wireOp",EDGE,"E166"),sQuery(id+"F48.wireOp",EDGE,"E167"),sQuery(id+"F48.wireOp",EDGE,"E168"),sQuery(id+"F48.wireOp",EDGE,"E169"),sQuery(id+"F48.wireOp",EDGE,"E170"),sQuery(id+"F48.wireOp",EDGE,"E171")])],"isStart":true});
            var sketch = newSketch(context, id + "F50", { "sketchPlane" : qUnion([Q0])});
            skLineSegment(sketch, "E174.0.4", {"start": v(80.74, -69.47) * mm, "end": v(144, 30.53) * mm});
            skLineSegment(sketch, "E174.0.5", {"start": v(16.76, -69.47) * mm, "end": v(80.74, -69.47) * mm});
            skLineSegment(sketch, "E174.0.6", {"start": v(4.06, -56.77) * mm, "end": v(16.76, -69.47) * mm});
            skLineSegment(sketch, "E174.0.7", {"start": v(4.06, 56.77) * mm, "end": v(4.06, -56.77) * mm});
            skLineSegment(sketch, "E174.0.8", {"start": v(16.76, 69.47) * mm, "end": v(4.06, 56.77) * mm});
            skLineSegment(sketch, "E174.0.9", {"start": v(77.22, 69.47) * mm, "end": v(16.76, 69.47) * mm});
            skLineSegment(sketch, "E174.0.10", {"start": v(77.22, 86.03) * mm, "end": v(77.22, 69.47) * mm});
            skLineSegment(sketch, "E175.0.0", {"start": v(144, 187.25) * mm, "end": v(77.22, 199.02) * mm});
            skLineSegment(sketch, "E175.0.1", {"start": v(77.22, 199.02) * mm, "end": v(77.22, 137.25) * mm});
            skLineSegment(sketch, "E175.0.8", {"start": v(144, 137.25) * mm, "end": v(144, 187.25) * mm});
            skLineSegment(sketch, "E176", {"start": v(77.22, 137.25) * mm, "end": v(144, 137.25) * mm});
            skSolve(sketch);
        }
        {
            var Q0;
            Q0=qSketchRegion(id+"F50",true);
            extrude(context, id + "F51", {"entities" : qUnion([Q0]), "depth" : 19 * mm});
        }
        {
            var Q0;
            Q0=makeQuery(id+"F51.opExtrude","SWEPT_FACE",FACE,{"disambiguationData":[OSD([sQuery(id+"F50.wireOp",EDGE,"E175.0.0")])]});
            var sketch = newSketch(context, id + "F52", { "sketchPlane" : qUnion([Q0])});
            skLineSegment(sketch, "E177", {"start": v(0, 185.79) * mm, "end": v(0, -149.3) * mm, "construction": true});
            skLineSegment(sketch, "E178.0", {"start": v(190, 185.79) * mm, "end": v(190, -149.3) * mm, "construction": true});
            skLineSegment(sketch, "E179.0.0", {"start": v(180, 109.52) * mm, "end": v(180, 34.38) * mm, "construction": true});
            skLineSegment(sketch, "E179.0.1", {"start": v(180, 34.38) * mm, "end": v(205.4, 34.38) * mm, "construction": true});
            skLineSegment(sketch, "E179.0.2", {"start": v(205.4, 34.38) * mm, "end": v(205.4, 109.52) * mm, "construction": true});
            skLineSegment(sketch, "E179.0.3", {"start": v(205.4, 109.52) * mm, "end": v(180, 109.52) * mm, "construction": true});
            skLineSegment(sketch, "E180.0", {"start": v(205.4, 69.52) * mm, "end": v(180, 69.52) * mm, "construction": true});
            skLineSegment(sketch, "E181.0", {"start": v(205.4, 94.52) * mm, "end": v(180, 94.52) * mm, "construction": true});
            skPoint(sketch, "E182", {"position": v(190, 94.52) * mm});
            skPoint(sketch, "E183", {"position": v(190, 69.52) * mm});
            skSolve(sketch);
        }
        {
            var Q0;
            Q0=sQuery(id+"F52.wireOp",VERTEX,"E182");
            var Q1;
            Q1=sQuery(id+"F52.wireOp",VERTEX,"E183");
            var Q2;
            Q2=makeQuery(id+"F51.opExtrude","SWEPT_BODY",BODY,{"disambiguationData":[OSD([sQuery(id+"F50.wireOp",EDGE,"E175.0.0"),sQuery(id+"F50.wireOp",EDGE,"E175.0.1"),sQuery(id+"F50.wireOp",EDGE,"E175.0.8"),sQuery(id+"F50.wireOp",EDGE,"E176")])]});
            hole(context, id + "F53", {"style" : HoleStyle.SIMPLE, "endStyle" : HoleEndStyle.BLIND, "standardTappedOrClearance" : lookupTablePath({ "standard" : "ISO", "engagement" : "75%", "pitch" : "1.5 mm", "size" : "M12", "type" : "Tapped" }), "standardBlindInLast" : lookupTablePath({ "standard" : "ISO", "engagement" : "75%", "pitch" : "1.5 mm", "size" : "M12", "type" : "Tapped" }), "holeDiameter" : 10.5 * mm, "holeDepth" : 30 * mm, "locations" : qUnion([Q0, Q1]), "scope" : qUnion([Q2]), "majorDiameter" : 12 * mm});
        }
        {
            var Q0;
            Q0=makeQuery(id+"F49.opExtrude","SWEPT_BODY",BODY,{"disambiguationData":[OSD([sQuery(id+"F48.wireOp",EDGE,"E159"),sQuery(id+"F48.wireOp",EDGE,"E162"),sQuery(id+"F48.wireOp",EDGE,"E163"),sQuery(id+"F48.wireOp",EDGE,"E164"),sQuery(id+"F48.wireOp",EDGE,"E165"),sQuery(id+"F48.wireOp",EDGE,"E166"),sQuery(id+"F48.wireOp",EDGE,"E167"),sQuery(id+"F48.wireOp",EDGE,"E168"),sQuery(id+"F48.wireOp",EDGE,"E169"),sQuery(id+"F48.wireOp",EDGE,"E170"),sQuery(id+"F48.wireOp",EDGE,"E171")])]});
            var Q1;
            Q1=makeQuery(id+"Fl3NnRKCw4Xixsh_5.opExtrude","SWEPT_BODY",BODY,{"disambiguationData":[OSD([sQuery(id+"F50.wireOp",EDGE,"E174.0.2"),sQuery(id+"F50.wireOp",EDGE,"L5QzTxGx-Pnf6-FATO-cNnD-iBCD0eLFIrfw"),sQuery(id+"F50.wireOp",EDGE,"wuJ0hKJl-j7K5-ufxr-qZVR-Fc0DleJu5Dkg"),sQuery(id+"F50.wireOp",EDGE,"Ftl8TeeW-pfTl-imrB-EIy6-TxBNQzbVambr")])]});
            var Q2;
            Q2=qCreatedBy(makeId("Right.planeOp"),FACE);
            mirror(context, id + "F54", {"entities" : qUnion([Q0, Q1]), "mirrorPlane" : qUnion([Q2])});
        }
        {
            var Q0;
            Q0=qCreatedBy(id+"F47.planeOp",FACE);
            cPlane(context, id + "F55", {"entities" : qUnion([Q0]), "cplaneType" : CPlaneType.OFFSET, "offset" : 350 * mm, "width" : 150 * mm, "height" : 150 * mm});
        }
        {
            var Q0;
            Q0=makeQuery(id+"F49.opExtrude","SWEPT_BODY",BODY,{"disambiguationData":[OSD([sQuery(id+"F48.wireOp",EDGE,"E159"),sQuery(id+"F48.wireOp",EDGE,"E162"),sQuery(id+"F48.wireOp",EDGE,"E163"),sQuery(id+"F48.wireOp",EDGE,"E164"),sQuery(id+"F48.wireOp",EDGE,"E165"),sQuery(id+"F48.wireOp",EDGE,"E166"),sQuery(id+"F48.wireOp",EDGE,"E167"),sQuery(id+"F48.wireOp",EDGE,"E168"),sQuery(id+"F48.wireOp",EDGE,"E169"),sQuery(id+"F48.wireOp",EDGE,"E170"),sQuery(id+"F48.wireOp",EDGE,"E171")])]});
            var Q1;
            Q1=makeQuery(id+"Fl3NnRKCw4Xixsh_5.opExtrude","SWEPT_BODY",BODY,{"disambiguationData":[OSD([sQuery(id+"F50.wireOp",EDGE,"E174.0.2"),sQuery(id+"F50.wireOp",EDGE,"L5QzTxGx-Pnf6-FATO-cNnD-iBCD0eLFIrfw"),sQuery(id+"F50.wireOp",EDGE,"wuJ0hKJl-j7K5-ufxr-qZVR-Fc0DleJu5Dkg"),sQuery(id+"F50.wireOp",EDGE,"Ftl8TeeW-pfTl-imrB-EIy6-TxBNQzbVambr")])]});
            var Q2;
            Q2=qCreatedBy(id+"F55.planeOp",FACE);
            mirror(context, id + "F56", {"entities" : qUnion([Q0, Q1]), "mirrorPlane" : qUnion([Q2])});
        }
        {
            var Q0;
            Q0=makeQuery(id+"F56.opPattern","COPY",BODY,{"derivedFrom":makeQuery(id+"F49.opExtrude","SWEPT_BODY",BODY,{"disambiguationData":[OSD([sQuery(id+"F48.wireOp",EDGE,"E159"),sQuery(id+"F48.wireOp",EDGE,"E162"),sQuery(id+"F48.wireOp",EDGE,"E163"),sQuery(id+"F48.wireOp",EDGE,"E164"),sQuery(id+"F48.wireOp",EDGE,"E165"),sQuery(id+"F48.wireOp",EDGE,"E166"),sQuery(id+"F48.wireOp",EDGE,"E167"),sQuery(id+"F48.wireOp",EDGE,"E168"),sQuery(id+"F48.wireOp",EDGE,"E169"),sQuery(id+"F48.wireOp",EDGE,"E170"),sQuery(id+"F48.wireOp",EDGE,"E171")])]}),"instanceName":"1"});
            var Q1;
            Q1=makeQuery(id+"F56.opPattern","COPY",BODY,{"derivedFrom":makeQuery(id+"Fl3NnRKCw4Xixsh_5.opExtrude","SWEPT_BODY",BODY,{"disambiguationData":[OSD([sQuery(id+"F50.wireOp",EDGE,"E174.0.2"),sQuery(id+"F50.wireOp",EDGE,"L5QzTxGx-Pnf6-FATO-cNnD-iBCD0eLFIrfw"),sQuery(id+"F50.wireOp",EDGE,"wuJ0hKJl-j7K5-ufxr-qZVR-Fc0DleJu5Dkg"),sQuery(id+"F50.wireOp",EDGE,"Ftl8TeeW-pfTl-imrB-EIy6-TxBNQzbVambr")])]}),"instanceName":"1"});
            var Q2;
            Q2=qCreatedBy(makeId("Right.planeOp"),FACE);
            mirror(context, id + "F57", {"entities" : qUnion([Q0, Q1]), "mirrorPlane" : qUnion([Q2])});
        }
        {
            var Q0;
            Q0=qCreatedBy(id+"F47.planeOp",FACE);
            var sketch = newSketch(context, id + "F58", { "sketchPlane" : qUnion([Q0])});
            skLineSegment(sketch, "E184", {"start": v(0, 263.92) * mm, "end": v(0, -250.39) * mm, "construction": true});
            skLineSegment(sketch, "E185.0", {"start": v(-206, 263.92) * mm, "end": v(-206, -250.39) * mm, "construction": true});
            skLineSegment(sketch, "E186.0.0", {"start": v(77.22, 81.03) * mm, "end": v(77.22, 69.47) * mm, "construction": true});
            skLineSegment(sketch, "E186.0.1", {"start": v(77.22, 69.47) * mm, "end": v(-77.22, 69.47) * mm, "construction": true});
            skLineSegment(sketch, "E186.0.2", {"start": v(-77.22, 69.47) * mm, "end": v(-77.22, 81.03) * mm, "construction": true});
            skLineSegment(sketch, "E186.0.3", {"start": v(-77.22, 81.03) * mm, "end": v(77.22, 81.03) * mm, "construction": true});
            skLineSegment(sketch, "E187.0.0", {"start": v(16.76, -69.47) * mm, "end": v(-16.76, -69.47) * mm, "construction": true});
            skArc(sketch, "E187.0.1", {"start": v(-16.76, -69.47) * mm, "mid": v(-7.78, -65.75) * mm, "end": v(-4.06, -56.77) * mm, "construction": true});
            skLineSegment(sketch, "E187.0.2", {"start": v(-4.06, -56.77) * mm, "end": v(-4.06, 56.77) * mm, "construction": true});
            skArc(sketch, "E187.0.3", {"start": v(-4.06, 56.77) * mm, "mid": v(-7.78, 65.75) * mm, "end": v(-16.76, 69.47) * mm, "construction": true});
            skLineSegment(sketch, "E187.0.4", {"start": v(-16.76, 69.47) * mm, "end": v(16.76, 69.47) * mm, "construction": true});
            skArc(sketch, "E187.0.5", {"start": v(16.76, 69.47) * mm, "mid": v(7.78, 65.75) * mm, "end": v(4.06, 56.77) * mm, "construction": true});
            skLineSegment(sketch, "E187.0.6", {"start": v(4.06, 56.77) * mm, "end": v(4.06, -56.77) * mm, "construction": true});
            skArc(sketch, "E187.0.7", {"start": v(4.06, -56.77) * mm, "mid": v(7.78, -65.75) * mm, "end": v(16.76, -69.47) * mm, "construction": true});
            skLineSegment(sketch, "E188.0.0", {"start": v(-77.22, -69.47) * mm, "end": v(77.22, -69.47) * mm, "construction": true});
            skLineSegment(sketch, "E188.0.1", {"start": v(77.22, -69.47) * mm, "end": v(77.22, -81.03) * mm, "construction": true});
            skLineSegment(sketch, "E188.0.2", {"start": v(77.22, -81.03) * mm, "end": v(-77.22, -81.03) * mm, "construction": true});
            skLineSegment(sketch, "E188.0.3", {"start": v(-77.22, -81.03) * mm, "end": v(-77.22, -69.47) * mm, "construction": true});
            skLineSegment(sketch, "E189.0", {"start": v(-206, 10.53) * mm, "end": v(77.22, 10.53) * mm, "construction": true});
            skLineSegment(sketch, "E190", {"start": v(-77.22, 69.47) * mm, "end": v(-16.76, 69.47) * mm});
            skLineSegment(sketch, "E191", {"start": v(-16.76, 69.47) * mm, "end": v(-4.06, 56.77) * mm});
            skLineSegment(sketch, "E192", {"start": v(-4.06, 56.77) * mm, "end": v(-4.06, -56.77) * mm});
            skLineSegment(sketch, "E193", {"start": v(-16.76, -69.47) * mm, "end": v(-4.06, -56.77) * mm});
            skLineSegment(sketch, "E194", {"start": v(-16.76, -69.47) * mm, "end": v(-77.22, -69.47) * mm});
            skLineSegment(sketch, "E195", {"start": v(-77.22, -69.47) * mm, "end": v(-206, 10.53) * mm});
            skLineSegment(sketch, "E196", {"start": v(-77.22, 69.47) * mm, "end": v(-77.22, 185.97) * mm});
            skLineSegment(sketch, "E197.0.0", {"start": v(-60, 81.03) * mm, "end": v(-60, 185.97) * mm});
            skLineSegment(sketch, "E197.0.1", {"start": v(-60, 185.97) * mm, "end": v(-22.5, 185.97) * mm});
            skLineSegment(sketch, "E197.0.2", {"start": v(-22.5, 185.97) * mm, "end": v(-22.5, 168.97) * mm});
            skArc(sketch, "E197.0.3", {"start": v(-22.5, 168.97) * mm, "mid": v(0, 146.47) * mm, "end": v(22.5, 168.97) * mm});
            skLineSegment(sketch, "E197.0.4", {"start": v(22.5, 168.97) * mm, "end": v(22.5, 185.97) * mm});
            skLineSegment(sketch, "E197.0.7", {"start": v(60, 81.03) * mm, "end": v(-60, 81.03) * mm});
            skPoint(sketch, "E197.0.6.start.orphan", {"position": v(60, 185.97) * mm});
            skLineSegment(sketch, "E198", {"start": v(-77.22, 185.97) * mm, "end": v(-222.54, 185.97) * mm, "construction": true});
            skLineSegment(sketch, "E199", {"start": v(-77.22, 185.97) * mm, "end": v(-206, 111.62) * mm});
            skLineSegment(sketch, "E200", {"start": v(-206, 111.62) * mm, "end": v(-206, 10.53) * mm});
            skSolve(sketch);
        }
        {
            var Q0;
            Q0=qSketchRegion(id+"F58",true);
            extrude(context, id + "F59", {"entities" : qUnion([Q0]), "oppositeDirection" : true, "depth" : 16 * mm});
        }
        {
            var Q0;
            Q0=makeQuery(id+"F59.opExtrude","CAP_FACE",FACE,{"disambiguationData":[OSD([sQuery(id+"F58.wireOp",EDGE,"E190"),sQuery(id+"F58.wireOp",EDGE,"E191"),sQuery(id+"F58.wireOp",EDGE,"E192"),sQuery(id+"F58.wireOp",EDGE,"E193"),sQuery(id+"F58.wireOp",EDGE,"E194"),sQuery(id+"F58.wireOp",EDGE,"E195"),sQuery(id+"F58.wireOp",EDGE,"E196"),sQuery(id+"F58.wireOp",EDGE,"E199"),sQuery(id+"F58.wireOp",EDGE,"E200")])],"isStart":false});
            var sketch = newSketch(context, id + "F60", { "sketchPlane" : qUnion([Q0])});
            skLineSegment(sketch, "E201.0.0", {"start": v(206, 111.62) * mm, "end": v(77.22, 185.97) * mm, "construction": true});
            skLineSegment(sketch, "E201.0.1", {"start": v(77.22, 185.97) * mm, "end": v(77.22, 69.47) * mm, "construction": true});
            skLineSegment(sketch, "E201.0.2", {"start": v(77.22, 69.47) * mm, "end": v(16.76, 69.47) * mm, "construction": true});
            skLineSegment(sketch, "E201.0.3", {"start": v(16.76, 69.47) * mm, "end": v(4.06, 56.77) * mm, "construction": true});
            skLineSegment(sketch, "E201.0.4", {"start": v(4.06, 56.77) * mm, "end": v(4.06, -56.77) * mm, "construction": true});
            skLineSegment(sketch, "E201.0.5", {"start": v(4.06, -56.77) * mm, "end": v(16.76, -69.47) * mm, "construction": true});
            skLineSegment(sketch, "E201.0.6", {"start": v(16.76, -69.47) * mm, "end": v(77.22, -69.47) * mm, "construction": true});
            skLineSegment(sketch, "E201.0.7", {"start": v(77.22, -69.47) * mm, "end": v(206, 10.53) * mm, "construction": true});
            skLineSegment(sketch, "E201.0.8", {"start": v(206, 10.53) * mm, "end": v(206, 111.62) * mm, "construction": true});
            skLineSegment(sketch, "E202.0", {"start": v(191, 85.64) * mm, "end": v(62.22, 160) * mm, "construction": true});
            skLineSegment(sketch, "E203", {"start": v(191, 85.64) * mm, "end": v(206, 111.62) * mm, "construction": true});
            skLineSegment(sketch, "E204.0", {"start": v(178, 93.14) * mm, "end": v(193, 119.12) * mm, "construction": true});
            skLineSegment(sketch, "E205.0", {"start": v(100.07, 138.14) * mm, "end": v(115.07, 164.12) * mm, "construction": true});
            skPoint(sketch, "E206", {"position": v(100.07, 138.14) * mm});
            skPoint(sketch, "E207", {"position": v(178, 93.14) * mm});
            skSolve(sketch);
        }
        {
            var Q0;
            Q0=sQuery(id+"F60.wireOp",VERTEX,"E206");
            var Q1;
            Q1=sQuery(id+"F60.wireOp",VERTEX,"E207");
            var Q2;
            Q2=makeQuery(id+"F59.opExtrude","SWEPT_BODY",BODY,{"disambiguationData":[OSD([sQuery(id+"F58.wireOp",EDGE,"E190"),sQuery(id+"F58.wireOp",EDGE,"E191"),sQuery(id+"F58.wireOp",EDGE,"E192"),sQuery(id+"F58.wireOp",EDGE,"E193"),sQuery(id+"F58.wireOp",EDGE,"E194"),sQuery(id+"F58.wireOp",EDGE,"E195"),sQuery(id+"F58.wireOp",EDGE,"E196"),sQuery(id+"F58.wireOp",EDGE,"E199"),sQuery(id+"F58.wireOp",EDGE,"E200")])]});
            hole(context, id + "F61", {"style" : HoleStyle.SIMPLE, "endStyle" : HoleEndStyle.BLIND, "standardTappedOrClearance" : lookupTablePath({ "standard" : "ISO", "size" : "12", "type" : "Drilled" }), "standardBlindInLast" : lookupTablePath({ "standard" : "ISO", "size" : "12", "type" : "Drilled" }), "holeDiameter" : 12 * mm, "holeDepth" : 30 * mm, "locations" : qUnion([Q0, Q1]), "scope" : qUnion([Q2])});
        }
        {
            var Q0;
            Q0=makeQuery(id+"F59.opExtrude","SWEPT_BODY",BODY,{"disambiguationData":[OSD([sQuery(id+"F58.wireOp",EDGE,"E190"),sQuery(id+"F58.wireOp",EDGE,"E191"),sQuery(id+"F58.wireOp",EDGE,"E192"),sQuery(id+"F58.wireOp",EDGE,"E193"),sQuery(id+"F58.wireOp",EDGE,"E194"),sQuery(id+"F58.wireOp",EDGE,"E195"),sQuery(id+"F58.wireOp",EDGE,"E196"),sQuery(id+"F58.wireOp",EDGE,"E199"),sQuery(id+"F58.wireOp",EDGE,"E200")])]});
            var Q1;
            Q1=qCreatedBy(makeId("Right.planeOp"),FACE);
            mirror(context, id + "F62", {"entities" : qUnion([Q0]), "mirrorPlane" : qUnion([Q1])});
        }
        {
            var Q0;
            Q0=makeQuery(id+"F59.opExtrude","SWEPT_BODY",BODY,{"disambiguationData":[OSD([sQuery(id+"F58.wireOp",EDGE,"E190"),sQuery(id+"F58.wireOp",EDGE,"E191"),sQuery(id+"F58.wireOp",EDGE,"E192"),sQuery(id+"F58.wireOp",EDGE,"E193"),sQuery(id+"F58.wireOp",EDGE,"E194"),sQuery(id+"F58.wireOp",EDGE,"E195"),sQuery(id+"F58.wireOp",EDGE,"E196"),sQuery(id+"F58.wireOp",EDGE,"E199"),sQuery(id+"F58.wireOp",EDGE,"E200")])]});
            var Q1;
            Q1=qCreatedBy(id+"F55.planeOp",FACE);
            mirror(context, id + "F63", {"entities" : qUnion([Q0]), "mirrorPlane" : qUnion([Q1])});
        }
        {
            var Q0;
            Q0=makeQuery(id+"F63.opPattern","COPY",BODY,{"derivedFrom":makeQuery(id+"F59.opExtrude","SWEPT_BODY",BODY,{"disambiguationData":[OSD([sQuery(id+"F58.wireOp",EDGE,"E190"),sQuery(id+"F58.wireOp",EDGE,"E191"),sQuery(id+"F58.wireOp",EDGE,"E192"),sQuery(id+"F58.wireOp",EDGE,"E193"),sQuery(id+"F58.wireOp",EDGE,"E194"),sQuery(id+"F58.wireOp",EDGE,"E195"),sQuery(id+"F58.wireOp",EDGE,"E196"),sQuery(id+"F58.wireOp",EDGE,"E199"),sQuery(id+"F58.wireOp",EDGE,"E200")])]}),"instanceName":"1"});
            var Q1;
            Q1=qCreatedBy(makeId("Right.planeOp"),FACE);
            mirror(context, id + "F64", {"operationType" : NewBodyOperationType.ADD, "entities" : qUnion([Q0]), "mirrorPlane" : qUnion([Q1])});
        }
        {
            var Q0;
            Q0=makeQuery(id+"F5.opExtrude","SWEPT_EDGE",EDGE,{"disambiguationData":[OSD([sQuery(id+"F4.wireOp",EDGE,"E50.bottom"),sQuery(id+"F4.wireOp",EDGE,"E50.right")])]});
            var Q1;
            Q1=makeQuery(id+"F5.opExtrude","SWEPT_EDGE",EDGE,{"disambiguationData":[OSD([sQuery(id+"F4.wireOp",EDGE,"E50.top"),sQuery(id+"F4.wireOp",EDGE,"E52.trimOffspring")])]});
            chamfer(context, id + "F65", {"entities" : qUnion([Q0, Q1]), "width" : 5 * mm, "tangentPropagation" : true});
        }
        {
            var Q0;
            Q0=makeQuery(id+"F29.opPattern","COPY",EDGE,{"derivedFrom":makeQuery(id+"F5.opExtrude","SWEPT_EDGE",EDGE,{"disambiguationData":[OSD([sQuery(id+"F4.wireOp",EDGE,"E50.bottom"),sQuery(id+"F4.wireOp",EDGE,"E50.right")])]}),"instanceName":"1"});
            var Q1;
            Q1=makeQuery(id+"F29.opPattern","COPY",EDGE,{"derivedFrom":makeQuery(id+"F5.opExtrude","SWEPT_EDGE",EDGE,{"disambiguationData":[OSD([sQuery(id+"F4.wireOp",EDGE,"E50.top"),sQuery(id+"F4.wireOp",EDGE,"E52.trimOffspring")])]}),"instanceName":"1"});
            chamfer(context, id + "F66", {"entities" : qUnion([Q0, Q1]), "width" : 5 * mm, "tangentPropagation" : true});
        }
        {
            var Q0;
            Q0=makeQuery(id+"F63.opPattern","COPY",FACE,{"derivedFrom":makeQuery(id+"F59.opExtrude","CAP_FACE",FACE,{"disambiguationData":[OSD([sQuery(id+"F58.wireOp",EDGE,"E190"),sQuery(id+"F58.wireOp",EDGE,"E191"),sQuery(id+"F58.wireOp",EDGE,"E192"),sQuery(id+"F58.wireOp",EDGE,"E193"),sQuery(id+"F58.wireOp",EDGE,"E194"),sQuery(id+"F58.wireOp",EDGE,"E195"),sQuery(id+"F58.wireOp",EDGE,"E196"),sQuery(id+"F58.wireOp",EDGE,"E199"),sQuery(id+"F58.wireOp",EDGE,"E200")])],"isStart":false}),"instanceName":"1"});
            var sketch = newSketch(context, id + "F67", { "sketchPlane" : qUnion([Q0])});
            skLineSegment(sketch, "E208.0", {"start": v(-35, -113.53) * mm, "end": v(-35, -148.53) * mm, "construction": true});
            skLineSegment(sketch, "E209", {"start": v(-35, -131.03) * mm, "end": v(-367.6, -131.03) * mm, "construction": true});
            skLineSegment(sketch, "E210.0", {"start": v(-35, -16.03) * mm, "end": v(-367.6, -16.03) * mm, "construction": true});
            skLineSegment(sketch, "E211.0", {"start": v(-35, 23.97) * mm, "end": v(-367.6, 23.97) * mm, "construction": true});
            skLineSegment(sketch, "E212", {"start": v(0, 332.63) * mm, "end": v(0, -263.23) * mm, "construction": true});
            skLineSegment(sketch, "E213.0", {"start": v(-140, 23.97) * mm, "end": v(-140, -16.03) * mm, "construction": true});
            skLineSegment(sketch, "E214.trimOffspring", {"start": v(-140, -131.03) * mm, "end": v(-140, -263.23) * mm, "construction": true});
            skLineSegment(sketch, "E215.bottom", {"start": v(-160, 23.97) * mm, "end": v(-120, 23.97) * mm});
            skLineSegment(sketch, "E215.top", {"start": v(-160, -16.03) * mm, "end": v(-120, -16.03) * mm});
            skLineSegment(sketch, "E215.left", {"start": v(-160, 23.97) * mm, "end": v(-160, -16.03) * mm});
            skLineSegment(sketch, "E215.right", {"start": v(-120, 23.97) * mm, "end": v(-120, -16.03) * mm});
            skPoint(sketch, "E215.middle", {"position": v(-140, 3.97) * mm});
            skSolve(sketch);
        }
        {
            var Q0;
            Q0=qSketchRegion(id+"F67",true);
            extrude(context, id + "F68", {"entities" : qUnion([Q0]), "depth" : 60 * mm});
        }
        {
            var Q0;
            Q0=makeQuery(id+"F68.opExtrude","SWEPT_FACE",FACE,{"disambiguationData":[OSD([sQuery(id+"F67.wireOp",EDGE,"E215.bottom")])]});
            var sketch = newSketch(context, id + "F69", { "sketchPlane" : qUnion([Q0])});
            skLineSegment(sketch, "E216.0", {"start": v(917.5, -35) * mm, "end": v(952.5, -35) * mm, "construction": true});
            skLineSegment(sketch, "E217", {"start": v(935, -120) * mm, "end": v(935, -160) * mm, "construction": true});
            skLineSegment(sketch, "E218.0.0", {"start": v(896, -120) * mm, "end": v(896, -160) * mm, "construction": true});
            skLineSegment(sketch, "E218.0.1", {"start": v(896, -160) * mm, "end": v(956, -160) * mm, "construction": true});
            skLineSegment(sketch, "E218.0.2", {"start": v(956, -160) * mm, "end": v(956, -120) * mm, "construction": true});
            skLineSegment(sketch, "E218.0.3", {"start": v(956, -120) * mm, "end": v(896, -120) * mm, "construction": true});
            skLineSegment(sketch, "E219", {"start": v(956, -140) * mm, "end": v(857.2, -140) * mm, "construction": true});
            skPoint(sketch, "E219.endSnap0", {"position": v(956, -140) * mm});
            skPoint(sketch, "E220.orphan", {"position": v(935, -35) * mm});
            skPoint(sketch, "E221", {"position": v(935, -140) * mm});
            skSolve(sketch);
        }
        {
            var Q0;
            Q0=sQuery(id+"F69.wireOp",VERTEX,"E221");
            var Q1;
            Q1=makeQuery(id+"F68.opExtrude","SWEPT_BODY",BODY,{"disambiguationData":[OSD([sQuery(id+"F67.wireOp",EDGE,"E215.bottom"),sQuery(id+"F67.wireOp",EDGE,"E215.top"),sQuery(id+"F67.wireOp",EDGE,"E215.left"),sQuery(id+"F67.wireOp",EDGE,"E215.right")])]});
            hole(context, id + "F70", {"style" : HoleStyle.SIMPLE, "endStyle" : HoleEndStyle.THROUGH, "standardTappedOrClearance" : lookupTablePath({ "standard" : "ISO", "size" : "20", "type" : "Drilled" }), "standardBlindInLast" : lookupTablePath({ "standard" : "ISO", "size" : "20", "type" : "Drilled" }), "holeDiameter" : 20 * mm, "locations" : qUnion([Q0]), "scope" : qUnion([Q1]), "isTappedThrough" : true});
        }
        {
            var Q0;
            Q0=makeQuery(id+"F68.opExtrude","SWEPT_FACE",FACE,{"disambiguationData":[OSD([sQuery(id+"F67.wireOp",EDGE,"E215.left")])]});
            var sketch = newSketch(context, id + "F71", { "sketchPlane" : qUnion([Q0])});
            skLineSegment(sketch, "E222.0", {"start": v(925, 23.97) * mm, "end": v(945, 23.97) * mm, "construction": true});
            skLineSegment(sketch, "E223", {"start": v(935, 23.97) * mm, "end": v(935, -16.03) * mm, "construction": true});
            skLineSegment(sketch, "E224.0", {"start": v(956, -16.03) * mm, "end": v(896, -16.03) * mm, "construction": true});
            skPoint(sketch, "E225", {"position": v(935, 3.97) * mm});
            skSolve(sketch);
        }
        {
            var Q0;
            Q0=sQuery(id+"F71.wireOp",VERTEX,"E225");
            var Q1;
            Q1=makeQuery(id+"F68.opExtrude","SWEPT_BODY",BODY,{"disambiguationData":[OSD([sQuery(id+"F67.wireOp",EDGE,"E215.bottom"),sQuery(id+"F67.wireOp",EDGE,"E215.top"),sQuery(id+"F67.wireOp",EDGE,"E215.left"),sQuery(id+"F67.wireOp",EDGE,"E215.right")])]});
            hole(context, id + "F72", {"style" : HoleStyle.SIMPLE, "endStyle" : HoleEndStyle.THROUGH, "standardTappedOrClearance" : lookupTablePath({ "standard" : "ISO", "size" : "8", "type" : "Drilled" }), "standardBlindInLast" : lookupTablePath({ "standard" : "ISO", "size" : "8", "type" : "Drilled" }), "holeDiameter" : 8 * mm, "locations" : qUnion([Q0]), "scope" : qUnion([Q1]), "isTappedThrough" : true});
        }
        {
            var Q0;
            Q0=makeQuery(id+"F68.opExtrude","SWEPT_BODY",BODY,{"disambiguationData":[OSD([sQuery(id+"F67.wireOp",EDGE,"E215.bottom"),sQuery(id+"F67.wireOp",EDGE,"E215.top"),sQuery(id+"F67.wireOp",EDGE,"E215.left"),sQuery(id+"F67.wireOp",EDGE,"E215.right")])]});
            var Q1;
            Q1=qCreatedBy(makeId("Right.planeOp"),FACE);
            mirror(context, id + "F73", {"entities" : qUnion([Q0]), "mirrorPlane" : qUnion([Q1])});
        }
        {
            var Q0;
            Q0=makeQuery(id+"F51.opExtrude","SWEPT_BODY",BODY,{"disambiguationData":[OSD([sQuery(id+"F50.wireOp",EDGE,"E175.0.0"),sQuery(id+"F50.wireOp",EDGE,"E175.0.1"),sQuery(id+"F50.wireOp",EDGE,"E175.0.8"),sQuery(id+"F50.wireOp",EDGE,"E176")])]});
            var Q1;
            Q1=qCreatedBy(id+"F55.planeOp",FACE);
            mirror(context, id + "F74", {"entities" : qUnion([Q0]), "mirrorPlane" : qUnion([Q1])});
        }
        {
            var Q0;
            Q0=makeQuery(id+"F51.opExtrude","SWEPT_BODY",BODY,{"disambiguationData":[OSD([sQuery(id+"F50.wireOp",EDGE,"E175.0.0"),sQuery(id+"F50.wireOp",EDGE,"E175.0.1"),sQuery(id+"F50.wireOp",EDGE,"E175.0.8"),sQuery(id+"F50.wireOp",EDGE,"E176")])]});
            var Q1;
            Q1=makeQuery(id+"F74.opPattern","COPY",BODY,{"derivedFrom":makeQuery(id+"F51.opExtrude","SWEPT_BODY",BODY,{"disambiguationData":[OSD([sQuery(id+"F50.wireOp",EDGE,"E175.0.0"),sQuery(id+"F50.wireOp",EDGE,"E175.0.1"),sQuery(id+"F50.wireOp",EDGE,"E175.0.8"),sQuery(id+"F50.wireOp",EDGE,"E176")])]}),"instanceName":"1"});
            var Q2;
            Q2=qCreatedBy(makeId("Right.planeOp"),FACE);
            mirror(context, id + "F75", {"entities" : qUnion([Q0, Q1]), "mirrorPlane" : qUnion([Q2])});
        }
    });
